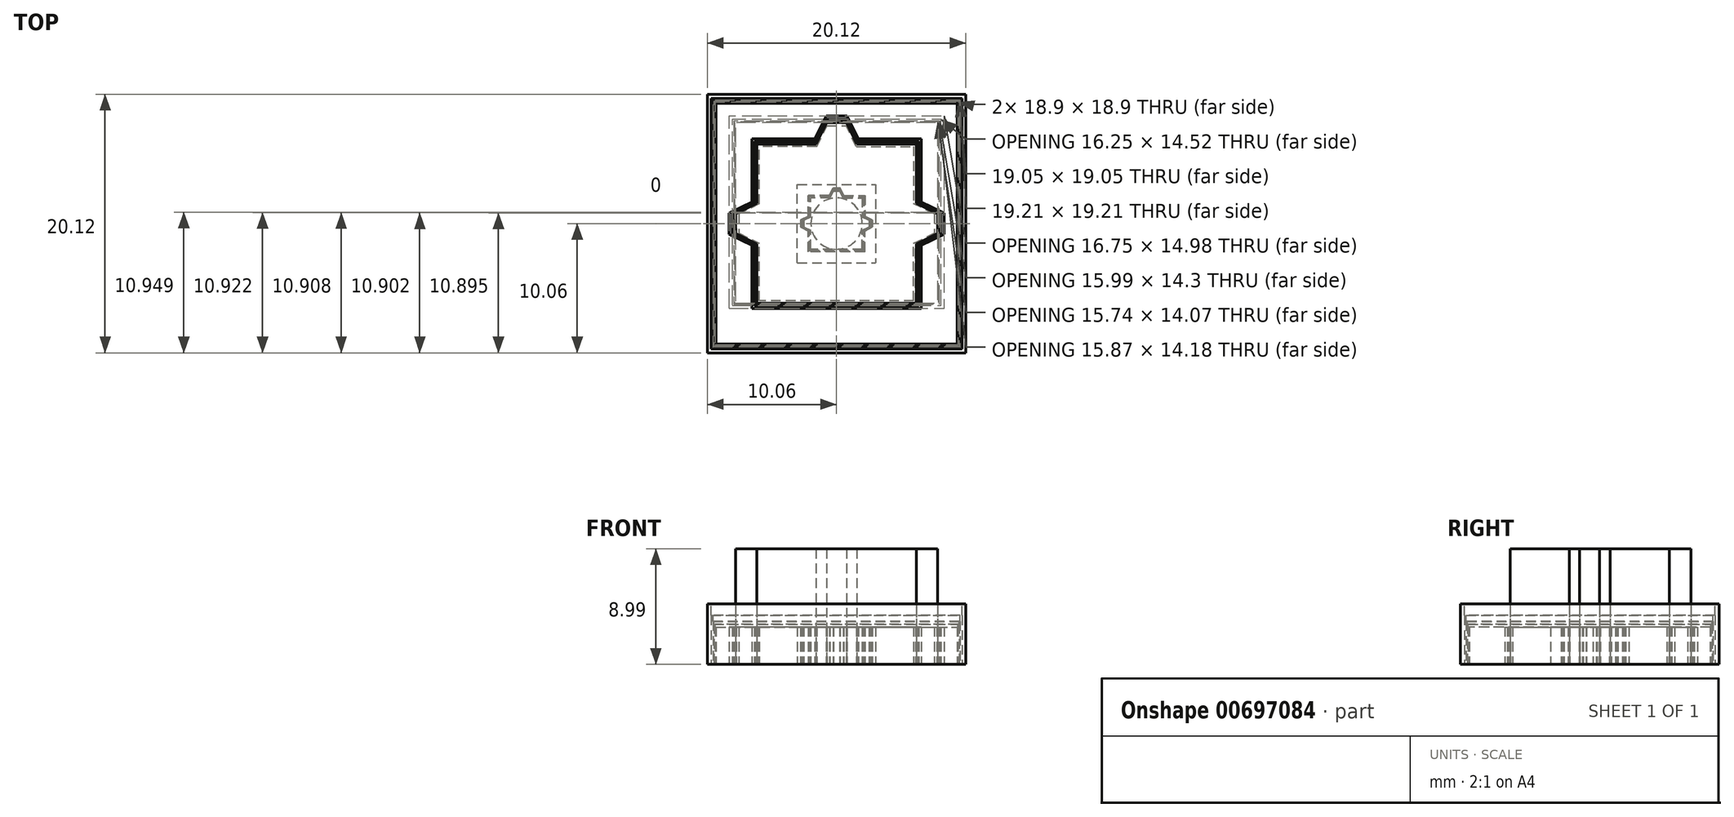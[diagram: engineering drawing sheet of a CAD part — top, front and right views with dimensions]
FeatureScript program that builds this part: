
annotation { "Feature Type Name" : "Feature", "Feature Type Description" : "" }
export const myFeature = defineFeature(function(context is Context, id is Id, definition is map)
    precondition{}
    {
        {
            assignVariable(context, id + "F0", {"name" : "pin_platform_thickness", "anyValue" : 4});
        }
        {
            assignVariable(context, id + "F1", {"name" : "pin_shaft_height", "anyValue" : 6});
        }
        {
            assignVariable(context, id + "F2", {"name" : "pin_hole_depth", "anyValue" : 5});
        }
        {
            var Q0;
            Q0=qCreatedBy(makeId("Top.planeOp"),FACE);
            var sketch = newSketch(context, id + "F3", { "sketchPlane" : qUnion([Q0])});
            skPoint(sketch, "E0.middle", {"position": v(0, 0) * mm});
            skCircle(sketch, "E1", {"center": v(0, 0) * mm, "radius": 2 * mm});
            skLineSegment(sketch, "E2", {"start": v(0, 0) * mm, "end": v(-2, 0) * mm});
            skLineSegment(sketch, "E3", {"start": v(-2, 0) * mm, "end": v(-2, 2) * mm});
            skLineSegment(sketch, "E4", {"start": v(0, 0) * mm, "end": v(0, 2) * mm});
            skLineSegment(sketch, "E5", {"start": v(0, 0) * mm, "end": v(2, 0) * mm});
            skLineSegment(sketch, "E6", {"start": v(0, 0) * mm, "end": v(0, -2) * mm});
            skLineSegment(sketch, "E7", {"start": v(0, -2) * mm, "end": v(2, 0) * mm});
            skLineSegment(sketch, "E8", {"start": v(2, 0) * mm, "end": v(0, 2) * mm});
            skLineSegment(sketch, "E9", {"start": v(0, 2) * mm, "end": v(-2, 0) * mm});
            skLineSegment(sketch, "E10", {"start": v(-2, 0) * mm, "end": v(0, -2) * mm});
            skLineSegment(sketch, "E11", {"start": v(0, -2) * mm, "end": v(-2, -2) * mm});
            skLineSegment(sketch, "E12", {"start": v(-2, -2) * mm, "end": v(-2, 0) * mm});
            skLineSegment(sketch, "E13", {"start": v(0, 2) * mm, "end": v(-2, 2) * mm});
            skLineSegment(sketch, "E14", {"start": v(0, 2) * mm, "end": v(2, 2) * mm});
            skLineSegment(sketch, "E15", {"start": v(2, 2) * mm, "end": v(2, 0) * mm});
            skLineSegment(sketch, "E16", {"start": v(2, -2) * mm, "end": v(0, -2) * mm});
            skLineSegment(sketch, "E17", {"start": v(2, -2) * mm, "end": v(2, 0) * mm});
            skLineSegment(sketch, "E18", {"start": v(0, 2) * mm, "end": v(0, 3.05) * mm});
            skLineSegment(sketch, "E19", {"start": v(0, 0) * mm, "end": v(0, 1) * mm});
            skLineSegment(sketch, "E20", {"start": v(0, 1) * mm, "end": v(1, 1) * mm});
            skLineSegment(sketch, "E21", {"start": v(1, 1) * mm, "end": v(0, 3.05) * mm});
            skLineSegment(sketch, "E22", {"start": v(0, 1) * mm, "end": v(-1, 1) * mm});
            skLineSegment(sketch, "E23", {"start": v(-1, 1) * mm, "end": v(0, 3.05) * mm});
            skLineSegment(sketch, "E24", {"start": v(1, 1) * mm, "end": v(1, 0) * mm});
            skLineSegment(sketch, "E25", {"start": v(1, 0) * mm, "end": v(1, -1) * mm});
            skLineSegment(sketch, "E26", {"start": v(1, -1) * mm, "end": v(3.05, 0) * mm});
            skLineSegment(sketch, "E27", {"start": v(3.05, 0) * mm, "end": v(1, 1) * mm});
            skLineSegment(sketch, "E28", {"start": v(1, -1) * mm, "end": v(-1, -1) * mm});
            skLineSegment(sketch, "E29", {"start": v(-1, -1) * mm, "end": v(-1, 1) * mm});
            skLineSegment(sketch, "E30", {"start": v(-1, 1) * mm, "end": v(-3.05, 0) * mm});
            skLineSegment(sketch, "E31", {"start": v(-3.05, 0) * mm, "end": v(-1, -1) * mm});
            skLineSegment(sketch, "E32", {"start": v(-1, -1) * mm, "end": v(0, -3.05) * mm});
            skLineSegment(sketch, "E33", {"start": v(0, -3.05) * mm, "end": v(1, -1) * mm});
            skLineSegment(sketch, "E34", {"start": v(2.54, 0.25) * mm, "end": v(2.54, -0.25) * mm});
            skLineSegment(sketch, "E35", {"start": v(-0.24, -2.55) * mm, "end": v(0.24, -2.55) * mm});
            skLineSegment(sketch, "E36", {"start": v(-2.54, 0.25) * mm, "end": v(-2.54, -0.25) * mm});
            skLineSegment(sketch, "E37", {"start": v(-0.25, 2.54) * mm, "end": v(0.25, 2.54) * mm});
            skLineSegment(sketch, "E38", {"start": v(-3.05, -3.05) * mm, "end": v(3.05, -3.05) * mm});
            skLineSegment(sketch, "E39", {"start": v(-3.05, -3.05) * mm, "end": v(-3.05, 3.05) * mm});
            skLineSegment(sketch, "E40", {"start": v(-3.05, 3.05) * mm, "end": v(3.05, 3.05) * mm});
            skLineSegment(sketch, "E41", {"start": v(3.05, 3.05) * mm, "end": v(3.05, -3.05) * mm});
            skCircle(sketch, "E42", {"center": v(0, 0) * mm, "radius": 0.38 * mm});
            skSolve(sketch);
        }
        {
            var Q0;
            {var subQ0=sQuery(id+"F3.wireOp",EDGE,"E23");var subQ3=sQuery(id+"F3.wireOp",EDGE,"E1");var subQ4=makeQuery(id+"F3.imprint","INTERSECT",VERTEX,{"derivedFrom":[subQ3,subQ0]});Q0=makeQuery(id+"F3.imprint","IMPRINT",FACE,{"disambiguationData":[TD([[makeQuery(id+"F3.imprint","IMPRINT",EDGE,{"disambiguationData":[TD([[subQ4,-1.0]])],"derivedFrom":subQ3}),-1.0]])]});}
            var Q1;
            {var subQ3=sQuery(id+"F3.wireOp",EDGE,"E23");var subQ5=sQuery(id+"F3.wireOp",EDGE,"E37");var subQ7=makeQuery(id+"F3.imprint","INTERSECT",VERTEX,{"derivedFrom":[subQ3,subQ5]});Q1=makeQuery(id+"F3.imprint","IMPRINT",FACE,{"disambiguationData":[TD([[makeQuery(id+"F3.imprint","IMPRINT",EDGE,{"disambiguationData":[TD([[subQ7,1.0]])],"derivedFrom":subQ3}),-1.0]])]});}
            var Q2;
            {var subQ3=sQuery(id+"F3.wireOp",EDGE,"E21");var subQ5=sQuery(id+"F3.wireOp",EDGE,"E37");var subQ6=makeQuery(id+"F3.imprint","INTERSECT",VERTEX,{"derivedFrom":[subQ3,subQ5]});Q2=makeQuery(id+"F3.imprint","IMPRINT",FACE,{"disambiguationData":[TD([[makeQuery(id+"F3.imprint","IMPRINT",EDGE,{"disambiguationData":[TD([[subQ6,1.0]])],"derivedFrom":subQ3}),1.0]])]});}
            var Q3;
            {var subQ3=sQuery(id+"F3.wireOp",EDGE,"E1");var subQ7=sQuery(id+"F3.wireOp",EDGE,"E27");var subQ9=makeQuery(id+"F3.imprint","INTERSECT",VERTEX,{"derivedFrom":[subQ3,subQ7]});Q3=makeQuery(id+"F3.imprint","IMPRINT",FACE,{"disambiguationData":[TD([[makeQuery(id+"F3.imprint","IMPRINT",EDGE,{"disambiguationData":[TD([[subQ9,-1.0]])],"derivedFrom":subQ3}),-1.0]])]});}
            var Q4;
            {var subQ0=sQuery(id+"F3.wireOp",EDGE,"E23");var subQ1=sQuery(id+"F3.wireOp",EDGE,"E1");var subQ2=makeQuery(id+"F3.imprint","INTERSECT",VERTEX,{"derivedFrom":[subQ1,subQ0]});Q4=makeQuery(id+"F3.imprint","IMPRINT",FACE,{"disambiguationData":[TD([[makeQuery(id+"F3.imprint","IMPRINT",EDGE,{"disambiguationData":[TD([[subQ2,-1.0]])],"derivedFrom":subQ1}),1.0]])]});}
            var Q5;
            {var subQ1=sQuery(id+"F3.wireOp",EDGE,"E1");var subQ3=sQuery(id+"F3.wireOp",EDGE,"E23");var subQ4=makeQuery(id+"F3.imprint","INTERSECT",VERTEX,{"derivedFrom":[subQ1,subQ3]});Q5=makeQuery(id+"F3.imprint","IMPRINT",FACE,{"disambiguationData":[TD([[makeQuery(id+"F3.imprint","IMPRINT",EDGE,{"disambiguationData":[TD([[subQ4,1.0]])],"derivedFrom":subQ3}),-1.0]])]});}
            var Q6;
            {var subQ1=sQuery(id+"F3.wireOp",EDGE,"E1");var subQ3=sQuery(id+"F3.wireOp",EDGE,"E21");var subQ4=makeQuery(id+"F3.imprint","INTERSECT",VERTEX,{"derivedFrom":[subQ1,subQ3]});Q6=makeQuery(id+"F3.imprint","IMPRINT",FACE,{"disambiguationData":[TD([[makeQuery(id+"F3.imprint","IMPRINT",EDGE,{"disambiguationData":[TD([[subQ4,1.0]])],"derivedFrom":subQ3}),1.0]])]});}
            var Q7;
            {var subQ0=sQuery(id+"F3.wireOp",EDGE,"E4");Q7=makeQuery(id+"F3.imprint","IMPRINT",FACE,{"disambiguationData":[TD([[makeQuery(id+"F3.imprint","IMPRINT",EDGE,{"derivedFrom":subQ0}),-1.0]])]});}
            var Q8;
            {var subQ0=sQuery(id+"F3.wireOp",EDGE,"E4");Q8=makeQuery(id+"F3.imprint","IMPRINT",FACE,{"disambiguationData":[TD([[makeQuery(id+"F3.imprint","IMPRINT",EDGE,{"derivedFrom":subQ0}),1.0]])]});}
            var Q9;
            {var subQ0=sQuery(id+"F3.wireOp",EDGE,"E19");Q9=makeQuery(id+"F3.imprint","IMPRINT",FACE,{"disambiguationData":[TD([[makeQuery(id+"F3.imprint","IMPRINT",EDGE,{"derivedFrom":subQ0}),1.0]])]});}
            var Q10;
            {var subQ1=sQuery(id+"F3.wireOp",EDGE,"E1");var subQ3=sQuery(id+"F3.wireOp",EDGE,"E30");var subQ4=makeQuery(id+"F3.imprint","INTERSECT",VERTEX,{"derivedFrom":[subQ1,subQ3]});Q10=makeQuery(id+"F3.imprint","IMPRINT",FACE,{"disambiguationData":[TD([[makeQuery(id+"F3.imprint","IMPRINT",EDGE,{"disambiguationData":[TD([[subQ4,1.0]])],"derivedFrom":subQ3}),1.0]])]});}
            var Q11;
            {var subQ1=sQuery(id+"F3.wireOp",EDGE,"E2");var subQ3=sQuery(id+"F3.wireOp",EDGE,"E29");var subQ4=makeQuery(id+"F3.imprint","INTERSECT",VERTEX,{"derivedFrom":[subQ1,subQ3]});Q11=makeQuery(id+"F3.imprint","IMPRINT",FACE,{"disambiguationData":[TD([[makeQuery(id+"F3.imprint","IMPRINT",EDGE,{"disambiguationData":[TD([[subQ4,-1.0]])],"derivedFrom":subQ3}),1.0]])]});}
            var Q12;
            {var subQ0=sQuery(id+"F3.wireOp",EDGE,"E19");Q12=makeQuery(id+"F3.imprint","IMPRINT",FACE,{"disambiguationData":[TD([[makeQuery(id+"F3.imprint","IMPRINT",EDGE,{"derivedFrom":subQ0}),-1.0]])]});}
            var Q13;
            {var subQ0=sQuery(id+"F3.wireOp",EDGE,"E27");var subQ1=sQuery(id+"F3.wireOp",EDGE,"E1");var subQ2=makeQuery(id+"F3.imprint","INTERSECT",VERTEX,{"derivedFrom":[subQ1,subQ0]});Q13=makeQuery(id+"F3.imprint","IMPRINT",FACE,{"disambiguationData":[TD([[makeQuery(id+"F3.imprint","IMPRINT",EDGE,{"disambiguationData":[TD([[subQ2,-1.0]])],"derivedFrom":subQ1}),1.0]])]});}
            var Q14;
            {var subQ0=sQuery(id+"F3.wireOp",EDGE,"E15");var subQ3=sQuery(id+"F3.wireOp",EDGE,"E27");var subQ5=makeQuery(id+"F3.imprint","INTERSECT",VERTEX,{"derivedFrom":[subQ0,subQ3]});Q14=makeQuery(id+"F3.imprint","IMPRINT",FACE,{"disambiguationData":[TD([[makeQuery(id+"F3.imprint","IMPRINT",EDGE,{"disambiguationData":[TD([[subQ5,-1.0]])],"derivedFrom":subQ3}),1.0]])]});}
            var Q15;
            {var subQ1=sQuery(id+"F3.wireOp",EDGE,"E1");var subQ3=sQuery(id+"F3.wireOp",EDGE,"E27");var subQ4=makeQuery(id+"F3.imprint","INTERSECT",VERTEX,{"derivedFrom":[subQ1,subQ3]});Q15=makeQuery(id+"F3.imprint","IMPRINT",FACE,{"disambiguationData":[TD([[makeQuery(id+"F3.imprint","IMPRINT",EDGE,{"disambiguationData":[TD([[subQ4,-1.0]])],"derivedFrom":subQ3}),1.0]])]});}
            var Q16;
            {var subQ3=sQuery(id+"F3.wireOp",EDGE,"E24");Q16=makeQuery(id+"F3.imprint","IMPRINT",FACE,{"disambiguationData":[TD([[makeQuery(id+"F3.imprint","IMPRINT",EDGE,{"derivedFrom":subQ3}),1.0]])]});}
            var Q17;
            {var subQ0=sQuery(id+"F3.wireOp",EDGE,"E3");var subQ3=sQuery(id+"F3.wireOp",EDGE,"E30");var subQ5=makeQuery(id+"F3.imprint","INTERSECT",VERTEX,{"derivedFrom":[subQ0,subQ3]});Q17=makeQuery(id+"F3.imprint","IMPRINT",FACE,{"disambiguationData":[TD([[makeQuery(id+"F3.imprint","IMPRINT",EDGE,{"disambiguationData":[TD([[subQ5,1.0]])],"derivedFrom":subQ3}),1.0]])]});}
            var Q18;
            {var subQ1=sQuery(id+"F3.wireOp",EDGE,"E2");var subQ3=sQuery(id+"F3.wireOp",EDGE,"E29");var subQ4=makeQuery(id+"F3.imprint","INTERSECT",VERTEX,{"derivedFrom":[subQ1,subQ3]});Q18=makeQuery(id+"F3.imprint","IMPRINT",FACE,{"disambiguationData":[TD([[makeQuery(id+"F3.imprint","IMPRINT",EDGE,{"disambiguationData":[TD([[subQ4,1.0]])],"derivedFrom":subQ3}),1.0]])]});}
            var Q19;
            {var subQ1=sQuery(id+"F3.wireOp",EDGE,"E1");var subQ3=sQuery(id+"F3.wireOp",EDGE,"E31");var subQ4=makeQuery(id+"F3.imprint","INTERSECT",VERTEX,{"derivedFrom":[subQ1,subQ3]});Q19=makeQuery(id+"F3.imprint","IMPRINT",FACE,{"disambiguationData":[TD([[makeQuery(id+"F3.imprint","IMPRINT",EDGE,{"disambiguationData":[TD([[subQ4,-1.0]])],"derivedFrom":subQ3}),1.0]])]});}
            var Q20;
            {var subQ0=sQuery(id+"F3.wireOp",EDGE,"E31");var subQ3=sQuery(id+"F3.wireOp",EDGE,"E1");var subQ4=makeQuery(id+"F3.imprint","INTERSECT",VERTEX,{"derivedFrom":[subQ3,subQ0]});Q20=makeQuery(id+"F3.imprint","IMPRINT",FACE,{"disambiguationData":[TD([[makeQuery(id+"F3.imprint","IMPRINT",EDGE,{"disambiguationData":[TD([[subQ4,-1.0]])],"derivedFrom":subQ3}),-1.0]])]});}
            var Q21;
            {var subQ0=sQuery(id+"F3.wireOp",EDGE,"E36");Q21=makeQuery(id+"F3.imprint","IMPRINT",FACE,{"disambiguationData":[TD([[makeQuery(id+"F3.imprint","IMPRINT",EDGE,{"derivedFrom":subQ0}),1.0]])]});}
            var Q22;
            {var subQ0=sQuery(id+"F3.wireOp",EDGE,"E12");var subQ3=sQuery(id+"F3.wireOp",EDGE,"E31");var subQ5=makeQuery(id+"F3.imprint","INTERSECT",VERTEX,{"derivedFrom":[subQ0,subQ3]});Q22=makeQuery(id+"F3.imprint","IMPRINT",FACE,{"disambiguationData":[TD([[makeQuery(id+"F3.imprint","IMPRINT",EDGE,{"disambiguationData":[TD([[subQ5,-1.0]])],"derivedFrom":subQ3}),1.0]])]});}
            var Q23;
            {var subQ1=sQuery(id+"F3.wireOp",EDGE,"E2");var subQ3=sQuery(id+"F3.wireOp",EDGE,"E29");var subQ4=makeQuery(id+"F3.imprint","INTERSECT",VERTEX,{"derivedFrom":[subQ1,subQ3]});Q23=makeQuery(id+"F3.imprint","IMPRINT",FACE,{"disambiguationData":[TD([[makeQuery(id+"F3.imprint","IMPRINT",EDGE,{"disambiguationData":[TD([[subQ4,1.0]])],"derivedFrom":subQ1}),1.0]])]});}
            var Q24;
            {var subQ3=sQuery(id+"F3.wireOp",EDGE,"E25");Q24=makeQuery(id+"F3.imprint","IMPRINT",FACE,{"disambiguationData":[TD([[makeQuery(id+"F3.imprint","IMPRINT",EDGE,{"derivedFrom":subQ3}),-1.0]])]});}
            var Q25;
            {var subQ1=sQuery(id+"F3.wireOp",EDGE,"E6");var subQ3=sQuery(id+"F3.wireOp",EDGE,"E28");var subQ4=makeQuery(id+"F3.imprint","INTERSECT",VERTEX,{"derivedFrom":[subQ1,subQ3]});Q25=makeQuery(id+"F3.imprint","IMPRINT",FACE,{"disambiguationData":[TD([[makeQuery(id+"F3.imprint","IMPRINT",EDGE,{"disambiguationData":[TD([[subQ4,1.0]])],"derivedFrom":subQ3}),1.0]])]});}
            var Q26;
            {var subQ1=sQuery(id+"F3.wireOp",EDGE,"E6");var subQ3=sQuery(id+"F3.wireOp",EDGE,"E28");var subQ4=makeQuery(id+"F3.imprint","INTERSECT",VERTEX,{"derivedFrom":[subQ1,subQ3]});Q26=makeQuery(id+"F3.imprint","IMPRINT",FACE,{"disambiguationData":[TD([[makeQuery(id+"F3.imprint","IMPRINT",EDGE,{"disambiguationData":[TD([[subQ4,-1.0]])],"derivedFrom":subQ3}),1.0]])]});}
            var Q27;
            {var subQ1=sQuery(id+"F3.wireOp",EDGE,"E1");var subQ3=sQuery(id+"F3.wireOp",EDGE,"E32");var subQ4=makeQuery(id+"F3.imprint","INTERSECT",VERTEX,{"derivedFrom":[subQ1,subQ3]});Q27=makeQuery(id+"F3.imprint","IMPRINT",FACE,{"disambiguationData":[TD([[makeQuery(id+"F3.imprint","IMPRINT",EDGE,{"disambiguationData":[TD([[subQ4,1.0]])],"derivedFrom":subQ3}),1.0]])]});}
            var Q28;
            {var subQ0=sQuery(id+"F3.wireOp",EDGE,"E31");var subQ1=sQuery(id+"F3.wireOp",EDGE,"E1");var subQ2=makeQuery(id+"F3.imprint","INTERSECT",VERTEX,{"derivedFrom":[subQ1,subQ0]});Q28=makeQuery(id+"F3.imprint","IMPRINT",FACE,{"disambiguationData":[TD([[makeQuery(id+"F3.imprint","IMPRINT",EDGE,{"disambiguationData":[TD([[subQ2,-1.0]])],"derivedFrom":subQ1}),1.0]])]});}
            var Q29;
            {var subQ1=sQuery(id+"F3.wireOp",EDGE,"E1");var subQ3=sQuery(id+"F3.wireOp",EDGE,"E33");var subQ4=makeQuery(id+"F3.imprint","INTERSECT",VERTEX,{"derivedFrom":[subQ1,subQ3]});Q29=makeQuery(id+"F3.imprint","IMPRINT",FACE,{"disambiguationData":[TD([[makeQuery(id+"F3.imprint","IMPRINT",EDGE,{"disambiguationData":[TD([[subQ4,-1.0]])],"derivedFrom":subQ3}),1.0]])]});}
            var Q30;
            {var subQ0=sQuery(id+"F3.wireOp",EDGE,"E33");var subQ1=sQuery(id+"F3.wireOp",EDGE,"E1");var subQ2=makeQuery(id+"F3.imprint","INTERSECT",VERTEX,{"derivedFrom":[subQ1,subQ0]});Q30=makeQuery(id+"F3.imprint","IMPRINT",FACE,{"disambiguationData":[TD([[makeQuery(id+"F3.imprint","IMPRINT",EDGE,{"disambiguationData":[TD([[subQ2,-1.0]])],"derivedFrom":subQ1}),1.0]])]});}
            var Q31;
            {var subQ1=sQuery(id+"F3.wireOp",EDGE,"E1");var subQ3=sQuery(id+"F3.wireOp",EDGE,"E26");var subQ4=makeQuery(id+"F3.imprint","INTERSECT",VERTEX,{"derivedFrom":[subQ1,subQ3]});Q31=makeQuery(id+"F3.imprint","IMPRINT",FACE,{"disambiguationData":[TD([[makeQuery(id+"F3.imprint","IMPRINT",EDGE,{"disambiguationData":[TD([[subQ4,1.0]])],"derivedFrom":subQ3}),1.0]])]});}
            var Q32;
            {var subQ3=sQuery(id+"F3.wireOp",EDGE,"E25");Q32=makeQuery(id+"F3.imprint","IMPRINT",FACE,{"disambiguationData":[TD([[makeQuery(id+"F3.imprint","IMPRINT",EDGE,{"derivedFrom":subQ3}),1.0]])]});}
            var Q33;
            {var subQ0=sQuery(id+"F3.wireOp",EDGE,"E17");var subQ3=sQuery(id+"F3.wireOp",EDGE,"E26");var subQ5=makeQuery(id+"F3.imprint","INTERSECT",VERTEX,{"derivedFrom":[subQ0,subQ3]});Q33=makeQuery(id+"F3.imprint","IMPRINT",FACE,{"disambiguationData":[TD([[makeQuery(id+"F3.imprint","IMPRINT",EDGE,{"disambiguationData":[TD([[subQ5,1.0]])],"derivedFrom":subQ3}),1.0]])]});}
            var Q34;
            {var subQ0=sQuery(id+"F3.wireOp",EDGE,"E34");Q34=makeQuery(id+"F3.imprint","IMPRINT",FACE,{"disambiguationData":[TD([[makeQuery(id+"F3.imprint","IMPRINT",EDGE,{"derivedFrom":subQ0}),-1.0]])]});}
            var Q35;
            {var subQ5=sQuery(id+"F3.wireOp",EDGE,"E1");var subQ7=sQuery(id+"F3.wireOp",EDGE,"E33");var subQ9=makeQuery(id+"F3.imprint","INTERSECT",VERTEX,{"derivedFrom":[subQ5,subQ7]});Q35=makeQuery(id+"F3.imprint","IMPRINT",FACE,{"disambiguationData":[TD([[makeQuery(id+"F3.imprint","IMPRINT",EDGE,{"disambiguationData":[TD([[subQ9,-1.0]])],"derivedFrom":subQ5}),-1.0]])]});}
            var Q36;
            {var subQ0=sQuery(id+"F3.wireOp",EDGE,"E35");Q36=makeQuery(id+"F3.imprint","IMPRINT",FACE,{"disambiguationData":[TD([[makeQuery(id+"F3.imprint","IMPRINT",EDGE,{"derivedFrom":subQ0}),1.0]])]});}
            var Q37;
            {var subQ0=sQuery(id+"F3.wireOp",EDGE,"E16");var subQ3=sQuery(id+"F3.wireOp",EDGE,"E33");var subQ5=makeQuery(id+"F3.imprint","INTERSECT",VERTEX,{"derivedFrom":[subQ0,subQ3]});Q37=makeQuery(id+"F3.imprint","IMPRINT",FACE,{"disambiguationData":[TD([[makeQuery(id+"F3.imprint","IMPRINT",EDGE,{"disambiguationData":[TD([[subQ5,-1.0]])],"derivedFrom":subQ3}),1.0]])]});}
            var Q38;
            {var subQ0=sQuery(id+"F3.wireOp",EDGE,"E11");var subQ3=sQuery(id+"F3.wireOp",EDGE,"E32");var subQ5=makeQuery(id+"F3.imprint","INTERSECT",VERTEX,{"derivedFrom":[subQ0,subQ3]});Q38=makeQuery(id+"F3.imprint","IMPRINT",FACE,{"disambiguationData":[TD([[makeQuery(id+"F3.imprint","IMPRINT",EDGE,{"disambiguationData":[TD([[subQ5,1.0]])],"derivedFrom":subQ3}),1.0]])]});}
            var Q39;
            {var subQ0=sQuery(id+"F3.wireOp",EDGE,"E14");var subQ3=sQuery(id+"F3.wireOp",EDGE,"E21");var subQ5=makeQuery(id+"F3.imprint","INTERSECT",VERTEX,{"derivedFrom":[subQ0,subQ3]});Q39=makeQuery(id+"F3.imprint","IMPRINT",FACE,{"disambiguationData":[TD([[makeQuery(id+"F3.imprint","IMPRINT",EDGE,{"disambiguationData":[TD([[subQ5,1.0]])],"derivedFrom":subQ3}),1.0]])]});}
            var Q40;
            {var subQ0=sQuery(id+"F3.wireOp",EDGE,"E13");var subQ3=sQuery(id+"F3.wireOp",EDGE,"E23");var subQ5=makeQuery(id+"F3.imprint","INTERSECT",VERTEX,{"derivedFrom":[subQ0,subQ3]});Q40=makeQuery(id+"F3.imprint","IMPRINT",FACE,{"disambiguationData":[TD([[makeQuery(id+"F3.imprint","IMPRINT",EDGE,{"disambiguationData":[TD([[subQ5,1.0]])],"derivedFrom":subQ3}),-1.0]])]});}
            extrude(context, id + "F4", {"entities" : qUnion([Q0, Q1, Q2, Q3, Q4, Q5, Q6, Q7, Q8, Q9, Q10, Q11, Q12, Q13, Q14, Q15, Q16, Q17, Q18, Q19, Q20, Q21, Q22, Q23, Q24, Q25, Q26, Q27, Q28, Q29, Q30, Q31, Q32, Q33, Q34, Q35, Q36, Q37, Q38, Q39, Q40]), "depth" : (getVariable(context, 'pin_platform_thickness')) * mm, "offsetDistance" : 25 * mm});
        }
        {
            var Q0;
            Q0=makeQuery(id+"F4.opExtrude","SWEPT_BODY",BODY,{"disambiguationData":[OSD([sQuery(id+"F3.wireOp",EDGE,"E3"),sQuery(id+"F3.wireOp",EDGE,"E11"),sQuery(id+"F3.wireOp",EDGE,"E12"),sQuery(id+"F3.wireOp",EDGE,"E13"),sQuery(id+"F3.wireOp",EDGE,"E14"),sQuery(id+"F3.wireOp",EDGE,"E15"),sQuery(id+"F3.wireOp",EDGE,"E16"),sQuery(id+"F3.wireOp",EDGE,"E17"),sQuery(id+"F3.wireOp",EDGE,"E21"),sQuery(id+"F3.wireOp",EDGE,"E23"),sQuery(id+"F3.wireOp",EDGE,"E26"),sQuery(id+"F3.wireOp",EDGE,"E27"),sQuery(id+"F3.wireOp",EDGE,"E30"),sQuery(id+"F3.wireOp",EDGE,"E31"),sQuery(id+"F3.wireOp",EDGE,"E32"),sQuery(id+"F3.wireOp",EDGE,"E33"),sQuery(id+"F3.wireOp",EDGE,"E34"),sQuery(id+"F3.wireOp",EDGE,"E35"),sQuery(id+"F3.wireOp",EDGE,"E36"),sQuery(id+"F3.wireOp",EDGE,"E37")])]});
            transform(context, id + "F5", {"entities" : qUnion([Q0]), "transformType" : TransformType.TRANSLATION_3D, "dx" : 0 * mm, "dy" : 0 * mm, "dz" : 0 * mm, "makeCopy" : true});
        }
        {
            var Q0;
            Q0=makeQuery(id+"F5.opPattern","COPY",BODY,{"derivedFrom":makeQuery(id+"F4.opExtrude","SWEPT_BODY",BODY,{"disambiguationData":[OSD([sQuery(id+"F3.wireOp",EDGE,"E3"),sQuery(id+"F3.wireOp",EDGE,"E11"),sQuery(id+"F3.wireOp",EDGE,"E12"),sQuery(id+"F3.wireOp",EDGE,"E13"),sQuery(id+"F3.wireOp",EDGE,"E14"),sQuery(id+"F3.wireOp",EDGE,"E15"),sQuery(id+"F3.wireOp",EDGE,"E16"),sQuery(id+"F3.wireOp",EDGE,"E17"),sQuery(id+"F3.wireOp",EDGE,"E21"),sQuery(id+"F3.wireOp",EDGE,"E23"),sQuery(id+"F3.wireOp",EDGE,"E26"),sQuery(id+"F3.wireOp",EDGE,"E27"),sQuery(id+"F3.wireOp",EDGE,"E30"),sQuery(id+"F3.wireOp",EDGE,"E31"),sQuery(id+"F3.wireOp",EDGE,"E32"),sQuery(id+"F3.wireOp",EDGE,"E33"),sQuery(id+"F3.wireOp",EDGE,"E34"),sQuery(id+"F3.wireOp",EDGE,"E35"),sQuery(id+"F3.wireOp",EDGE,"E36"),sQuery(id+"F3.wireOp",EDGE,"E37")])]}),"instanceName":"1"});
            var Q1;
            Q1=sQuery(id+"F3.wireOp",VERTEX,"E0.middle");
            transform(context, id + "F6", {"entities" : qUnion([Q0]), "transformType" : TransformType.SCALE_UNIFORMLY, "scale" : 1.1, "scalePoint" : qUnion([Q1]), "makeCopy" : false});
        }
        {
            var Q0;
            Q0=makeQuery(id+"F4.opExtrude","SWEPT_BODY",BODY,{"disambiguationData":[OSD([sQuery(id+"F3.wireOp",EDGE,"E3"),sQuery(id+"F3.wireOp",EDGE,"E11"),sQuery(id+"F3.wireOp",EDGE,"E12"),sQuery(id+"F3.wireOp",EDGE,"E13"),sQuery(id+"F3.wireOp",EDGE,"E14"),sQuery(id+"F3.wireOp",EDGE,"E15"),sQuery(id+"F3.wireOp",EDGE,"E16"),sQuery(id+"F3.wireOp",EDGE,"E17"),sQuery(id+"F3.wireOp",EDGE,"E21"),sQuery(id+"F3.wireOp",EDGE,"E23"),sQuery(id+"F3.wireOp",EDGE,"E26"),sQuery(id+"F3.wireOp",EDGE,"E27"),sQuery(id+"F3.wireOp",EDGE,"E30"),sQuery(id+"F3.wireOp",EDGE,"E31"),sQuery(id+"F3.wireOp",EDGE,"E32"),sQuery(id+"F3.wireOp",EDGE,"E33"),sQuery(id+"F3.wireOp",EDGE,"E34"),sQuery(id+"F3.wireOp",EDGE,"E35"),sQuery(id+"F3.wireOp",EDGE,"E36"),sQuery(id+"F3.wireOp",EDGE,"E37")])]});
            var Q1;
            Q1=makeQuery(id+"F5.opPattern","COPY",BODY,{"derivedFrom":makeQuery(id+"F4.opExtrude","SWEPT_BODY",BODY,{"disambiguationData":[OSD([sQuery(id+"F3.wireOp",EDGE,"E3"),sQuery(id+"F3.wireOp",EDGE,"E11"),sQuery(id+"F3.wireOp",EDGE,"E12"),sQuery(id+"F3.wireOp",EDGE,"E13"),sQuery(id+"F3.wireOp",EDGE,"E14"),sQuery(id+"F3.wireOp",EDGE,"E15"),sQuery(id+"F3.wireOp",EDGE,"E16"),sQuery(id+"F3.wireOp",EDGE,"E17"),sQuery(id+"F3.wireOp",EDGE,"E21"),sQuery(id+"F3.wireOp",EDGE,"E23"),sQuery(id+"F3.wireOp",EDGE,"E26"),sQuery(id+"F3.wireOp",EDGE,"E27"),sQuery(id+"F3.wireOp",EDGE,"E30"),sQuery(id+"F3.wireOp",EDGE,"E31"),sQuery(id+"F3.wireOp",EDGE,"E32"),sQuery(id+"F3.wireOp",EDGE,"E33"),sQuery(id+"F3.wireOp",EDGE,"E34"),sQuery(id+"F3.wireOp",EDGE,"E35"),sQuery(id+"F3.wireOp",EDGE,"E36"),sQuery(id+"F3.wireOp",EDGE,"E37")])]}),"instanceName":"1"});
            booleanBodies(context, id + "F7", {"operationType" : BooleanOperationType.SUBTRACTION, "tools" : qUnion([Q0]), "targets" : qUnion([Q1])});
        }
        {
            var Q0;
            Q0=makeQuery(id+"F5.opPattern","COPY",BODY,{"derivedFrom":makeQuery(id+"F4.opExtrude","SWEPT_BODY",BODY,{"disambiguationData":[OSD([sQuery(id+"F3.wireOp",EDGE,"E3"),sQuery(id+"F3.wireOp",EDGE,"E11"),sQuery(id+"F3.wireOp",EDGE,"E12"),sQuery(id+"F3.wireOp",EDGE,"E13"),sQuery(id+"F3.wireOp",EDGE,"E14"),sQuery(id+"F3.wireOp",EDGE,"E15"),sQuery(id+"F3.wireOp",EDGE,"E16"),sQuery(id+"F3.wireOp",EDGE,"E17"),sQuery(id+"F3.wireOp",EDGE,"E21"),sQuery(id+"F3.wireOp",EDGE,"E23"),sQuery(id+"F3.wireOp",EDGE,"E26"),sQuery(id+"F3.wireOp",EDGE,"E27"),sQuery(id+"F3.wireOp",EDGE,"E30"),sQuery(id+"F3.wireOp",EDGE,"E31"),sQuery(id+"F3.wireOp",EDGE,"E32"),sQuery(id+"F3.wireOp",EDGE,"E33"),sQuery(id+"F3.wireOp",EDGE,"E34"),sQuery(id+"F3.wireOp",EDGE,"E35"),sQuery(id+"F3.wireOp",EDGE,"E36"),sQuery(id+"F3.wireOp",EDGE,"E37")])]}),"instanceName":"1"});
            deleteBodies(context, id + "F8", {"entities" : qUnion([Q0])});
        }
        {
            var Q0;
            Q0 = qSketchRegion(id + "F3", true);
            var Q1;
            {var subQ0=sQuery(id+"F3.wireOp",EDGE,"E31");var subQ1=sQuery(id+"F3.wireOp",EDGE,"E1");var subQ2=makeQuery(id+"F3.imprint","INTERSECT",VERTEX,{"derivedFrom":[subQ1,subQ0]});Q1=makeQuery(id+"F3.imprint","IMPRINT",FACE,{"disambiguationData":[TD([[makeQuery(id+"F3.imprint","IMPRINT",EDGE,{"disambiguationData":[TD([[subQ2,-1.0]])],"derivedFrom":subQ1}),-1.0]])]});}
            var Q2;
            {var subQ1=sQuery(id+"F3.wireOp",EDGE,"E1");var subQ3=sQuery(id+"F3.wireOp",EDGE,"E32");var subQ4=makeQuery(id+"F3.imprint","INTERSECT",VERTEX,{"derivedFrom":[subQ1,subQ3]});Q2=makeQuery(id+"F3.imprint","IMPRINT",FACE,{"disambiguationData":[TD([[makeQuery(id+"F3.imprint","IMPRINT",EDGE,{"disambiguationData":[TD([[subQ4,1.0]])],"derivedFrom":subQ3}),1.0]])]});}
            var Q3;
            {var subQ1=sQuery(id+"F3.wireOp",EDGE,"E1");var subQ3=sQuery(id+"F3.wireOp",EDGE,"E33");var subQ4=makeQuery(id+"F3.imprint","INTERSECT",VERTEX,{"derivedFrom":[subQ1,subQ3]});Q3=makeQuery(id+"F3.imprint","IMPRINT",FACE,{"disambiguationData":[TD([[makeQuery(id+"F3.imprint","IMPRINT",EDGE,{"disambiguationData":[TD([[subQ4,-1.0]])],"derivedFrom":subQ3}),1.0]])]});}
            var Q4;
            {var subQ0=sQuery(id+"F3.wireOp",EDGE,"E33");var subQ1=sQuery(id+"F3.wireOp",EDGE,"E1");var subQ2=makeQuery(id+"F3.imprint","INTERSECT",VERTEX,{"derivedFrom":[subQ1,subQ0]});Q4=makeQuery(id+"F3.imprint","IMPRINT",FACE,{"disambiguationData":[TD([[makeQuery(id+"F3.imprint","IMPRINT",EDGE,{"disambiguationData":[TD([[subQ2,-1.0]])],"derivedFrom":subQ1}),1.0]])]});}
            var Q5;
            {var subQ5=sQuery(id+"F3.wireOp",EDGE,"E1");var subQ7=sQuery(id+"F3.wireOp",EDGE,"E33");var subQ9=makeQuery(id+"F3.imprint","INTERSECT",VERTEX,{"derivedFrom":[subQ5,subQ7]});Q5=makeQuery(id+"F3.imprint","IMPRINT",FACE,{"disambiguationData":[TD([[makeQuery(id+"F3.imprint","IMPRINT",EDGE,{"disambiguationData":[TD([[subQ9,-1.0]])],"derivedFrom":subQ5}),-1.0]])]});}
            var Q6;
            {var subQ0=sQuery(id+"F3.wireOp",EDGE,"E31");var subQ1=sQuery(id+"F3.wireOp",EDGE,"E1");var subQ2=makeQuery(id+"F3.imprint","INTERSECT",VERTEX,{"derivedFrom":[subQ1,subQ0]});Q6=makeQuery(id+"F3.imprint","IMPRINT",FACE,{"disambiguationData":[TD([[makeQuery(id+"F3.imprint","IMPRINT",EDGE,{"disambiguationData":[TD([[subQ2,-1.0]])],"derivedFrom":subQ1}),1.0]])]});}
            var Q7;
            {var subQ0=sQuery(id+"F3.wireOp",EDGE,"E19");Q7=makeQuery(id+"F3.imprint","IMPRINT",FACE,{"disambiguationData":[TD([[makeQuery(id+"F3.imprint","IMPRINT",EDGE,{"derivedFrom":subQ0}),-1.0]])]});}
            var Q8;
            {var subQ0=sQuery(id+"F3.wireOp",EDGE,"E19");Q8=makeQuery(id+"F3.imprint","IMPRINT",FACE,{"disambiguationData":[TD([[makeQuery(id+"F3.imprint","IMPRINT",EDGE,{"derivedFrom":subQ0}),1.0]])]});}
            var Q9;
            {var subQ1=sQuery(id+"F3.wireOp",EDGE,"E2");var subQ3=sQuery(id+"F3.wireOp",EDGE,"E29");var subQ4=makeQuery(id+"F3.imprint","INTERSECT",VERTEX,{"derivedFrom":[subQ1,subQ3]});Q9=makeQuery(id+"F3.imprint","IMPRINT",FACE,{"disambiguationData":[TD([[makeQuery(id+"F3.imprint","IMPRINT",EDGE,{"disambiguationData":[TD([[subQ4,-1.0]])],"derivedFrom":subQ3}),1.0]])]});}
            var Q10;
            {var subQ1=sQuery(id+"F3.wireOp",EDGE,"E1");var subQ3=sQuery(id+"F3.wireOp",EDGE,"E30");var subQ4=makeQuery(id+"F3.imprint","INTERSECT",VERTEX,{"derivedFrom":[subQ1,subQ3]});Q10=makeQuery(id+"F3.imprint","IMPRINT",FACE,{"disambiguationData":[TD([[makeQuery(id+"F3.imprint","IMPRINT",EDGE,{"disambiguationData":[TD([[subQ4,1.0]])],"derivedFrom":subQ3}),1.0]])]});}
            var Q11;
            {var subQ0=sQuery(id+"F3.wireOp",EDGE,"E23");var subQ1=sQuery(id+"F3.wireOp",EDGE,"E1");var subQ2=makeQuery(id+"F3.imprint","INTERSECT",VERTEX,{"derivedFrom":[subQ1,subQ0]});Q11=makeQuery(id+"F3.imprint","IMPRINT",FACE,{"disambiguationData":[TD([[makeQuery(id+"F3.imprint","IMPRINT",EDGE,{"disambiguationData":[TD([[subQ2,-1.0]])],"derivedFrom":subQ1}),1.0]])]});}
            var Q12;
            {var subQ0=sQuery(id+"F3.wireOp",EDGE,"E23");var subQ1=sQuery(id+"F3.wireOp",EDGE,"E1");var subQ2=makeQuery(id+"F3.imprint","INTERSECT",VERTEX,{"derivedFrom":[subQ1,subQ0]});Q12=makeQuery(id+"F3.imprint","IMPRINT",FACE,{"disambiguationData":[TD([[makeQuery(id+"F3.imprint","IMPRINT",EDGE,{"disambiguationData":[TD([[subQ2,-1.0]])],"derivedFrom":subQ1}),-1.0]])]});}
            var Q13;
            {var subQ1=sQuery(id+"F3.wireOp",EDGE,"E1");var subQ3=sQuery(id+"F3.wireOp",EDGE,"E23");var subQ4=makeQuery(id+"F3.imprint","INTERSECT",VERTEX,{"derivedFrom":[subQ1,subQ3]});Q13=makeQuery(id+"F3.imprint","IMPRINT",FACE,{"disambiguationData":[TD([[makeQuery(id+"F3.imprint","IMPRINT",EDGE,{"disambiguationData":[TD([[subQ4,1.0]])],"derivedFrom":subQ3}),-1.0]])]});}
            var Q14;
            {var subQ3=sQuery(id+"F3.wireOp",EDGE,"E23");var subQ5=sQuery(id+"F3.wireOp",EDGE,"E37");var subQ7=makeQuery(id+"F3.imprint","INTERSECT",VERTEX,{"derivedFrom":[subQ3,subQ5]});Q14=makeQuery(id+"F3.imprint","IMPRINT",FACE,{"disambiguationData":[TD([[makeQuery(id+"F3.imprint","IMPRINT",EDGE,{"disambiguationData":[TD([[subQ7,1.0]])],"derivedFrom":subQ3}),-1.0]])]});}
            var Q15;
            {var subQ1=sQuery(id+"F3.wireOp",EDGE,"E1");var subQ3=sQuery(id+"F3.wireOp",EDGE,"E21");var subQ4=makeQuery(id+"F3.imprint","INTERSECT",VERTEX,{"derivedFrom":[subQ1,subQ3]});Q15=makeQuery(id+"F3.imprint","IMPRINT",FACE,{"disambiguationData":[TD([[makeQuery(id+"F3.imprint","IMPRINT",EDGE,{"disambiguationData":[TD([[subQ4,1.0]])],"derivedFrom":subQ3}),1.0]])]});}
            var Q16;
            {var subQ0=sQuery(id+"F3.wireOp",EDGE,"E4");Q16=makeQuery(id+"F3.imprint","IMPRINT",FACE,{"disambiguationData":[TD([[makeQuery(id+"F3.imprint","IMPRINT",EDGE,{"derivedFrom":subQ0}),-1.0]])]});}
            var Q17;
            {var subQ0=sQuery(id+"F3.wireOp",EDGE,"E4");Q17=makeQuery(id+"F3.imprint","IMPRINT",FACE,{"disambiguationData":[TD([[makeQuery(id+"F3.imprint","IMPRINT",EDGE,{"derivedFrom":subQ0}),1.0]])]});}
            var Q18;
            {var subQ0=sQuery(id+"F3.wireOp",EDGE,"E27");var subQ1=sQuery(id+"F3.wireOp",EDGE,"E1");var subQ2=makeQuery(id+"F3.imprint","INTERSECT",VERTEX,{"derivedFrom":[subQ1,subQ0]});Q18=makeQuery(id+"F3.imprint","IMPRINT",FACE,{"disambiguationData":[TD([[makeQuery(id+"F3.imprint","IMPRINT",EDGE,{"disambiguationData":[TD([[subQ2,-1.0]])],"derivedFrom":subQ1}),1.0]])]});}
            var Q19;
            {var subQ1=sQuery(id+"F3.wireOp",EDGE,"E1");var subQ7=sQuery(id+"F3.wireOp",EDGE,"E27");var subQ9=makeQuery(id+"F3.imprint","INTERSECT",VERTEX,{"derivedFrom":[subQ1,subQ7]});Q19=makeQuery(id+"F3.imprint","IMPRINT",FACE,{"disambiguationData":[TD([[makeQuery(id+"F3.imprint","IMPRINT",EDGE,{"disambiguationData":[TD([[subQ9,-1.0]])],"derivedFrom":subQ1}),-1.0]])]});}
            var Q20;
            {var subQ3=sQuery(id+"F3.wireOp",EDGE,"E24");Q20=makeQuery(id+"F3.imprint","IMPRINT",FACE,{"disambiguationData":[TD([[makeQuery(id+"F3.imprint","IMPRINT",EDGE,{"derivedFrom":subQ3}),1.0]])]});}
            var Q21;
            {var subQ1=sQuery(id+"F3.wireOp",EDGE,"E1");var subQ3=sQuery(id+"F3.wireOp",EDGE,"E27");var subQ4=makeQuery(id+"F3.imprint","INTERSECT",VERTEX,{"derivedFrom":[subQ1,subQ3]});Q21=makeQuery(id+"F3.imprint","IMPRINT",FACE,{"disambiguationData":[TD([[makeQuery(id+"F3.imprint","IMPRINT",EDGE,{"disambiguationData":[TD([[subQ4,-1.0]])],"derivedFrom":subQ3}),1.0]])]});}
            var Q22;
            {var subQ1=sQuery(id+"F3.wireOp",EDGE,"E1");var subQ3=sQuery(id+"F3.wireOp",EDGE,"E26");var subQ4=makeQuery(id+"F3.imprint","INTERSECT",VERTEX,{"derivedFrom":[subQ1,subQ3]});Q22=makeQuery(id+"F3.imprint","IMPRINT",FACE,{"disambiguationData":[TD([[makeQuery(id+"F3.imprint","IMPRINT",EDGE,{"disambiguationData":[TD([[subQ4,1.0]])],"derivedFrom":subQ3}),1.0]])]});}
            var Q23;
            {var subQ3=sQuery(id+"F3.wireOp",EDGE,"E25");Q23=makeQuery(id+"F3.imprint","IMPRINT",FACE,{"disambiguationData":[TD([[makeQuery(id+"F3.imprint","IMPRINT",EDGE,{"derivedFrom":subQ3}),1.0]])]});}
            var Q24;
            {var subQ3=sQuery(id+"F3.wireOp",EDGE,"E21");var subQ5=sQuery(id+"F3.wireOp",EDGE,"E37");var subQ6=makeQuery(id+"F3.imprint","INTERSECT",VERTEX,{"derivedFrom":[subQ3,subQ5]});Q24=makeQuery(id+"F3.imprint","IMPRINT",FACE,{"disambiguationData":[TD([[makeQuery(id+"F3.imprint","IMPRINT",EDGE,{"disambiguationData":[TD([[subQ6,1.0]])],"derivedFrom":subQ3}),1.0]])]});}
            var Q25;
            {var subQ1=sQuery(id+"F3.wireOp",EDGE,"E1");var subQ3=sQuery(id+"F3.wireOp",EDGE,"E21");var subQ4=makeQuery(id+"F3.imprint","INTERSECT",VERTEX,{"derivedFrom":[subQ1,subQ3]});Q25=makeQuery(id+"F3.imprint","IMPRINT",FACE,{"disambiguationData":[TD([[makeQuery(id+"F3.imprint","IMPRINT",EDGE,{"disambiguationData":[TD([[subQ4,-1.0]])],"derivedFrom":subQ3}),1.0]])]});}
            var Q26;
            {var subQ1=sQuery(id+"F3.wireOp",EDGE,"E1");var subQ3=sQuery(id+"F3.wireOp",EDGE,"E23");var subQ4=makeQuery(id+"F3.imprint","INTERSECT",VERTEX,{"derivedFrom":[subQ1,subQ3]});Q26=makeQuery(id+"F3.imprint","IMPRINT",FACE,{"disambiguationData":[TD([[makeQuery(id+"F3.imprint","IMPRINT",EDGE,{"disambiguationData":[TD([[subQ4,-1.0]])],"derivedFrom":subQ3}),-1.0]])]});}
            var Q27;
            {var subQ1=sQuery(id+"F3.wireOp",EDGE,"E1");var subQ3=sQuery(id+"F3.wireOp",EDGE,"E27");var subQ4=makeQuery(id+"F3.imprint","INTERSECT",VERTEX,{"derivedFrom":[subQ1,subQ3]});Q27=makeQuery(id+"F3.imprint","IMPRINT",FACE,{"disambiguationData":[TD([[makeQuery(id+"F3.imprint","IMPRINT",EDGE,{"disambiguationData":[TD([[subQ4,1.0]])],"derivedFrom":subQ3}),1.0]])]});}
            var Q28;
            {var subQ1=sQuery(id+"F3.wireOp",EDGE,"E1");var subQ3=sQuery(id+"F3.wireOp",EDGE,"E26");var subQ4=makeQuery(id+"F3.imprint","INTERSECT",VERTEX,{"derivedFrom":[subQ1,subQ3]});Q28=makeQuery(id+"F3.imprint","IMPRINT",FACE,{"disambiguationData":[TD([[makeQuery(id+"F3.imprint","IMPRINT",EDGE,{"disambiguationData":[TD([[subQ4,-1.0]])],"derivedFrom":subQ3}),1.0]])]});}
            var Q29;
            {var subQ3=sQuery(id+"F3.wireOp",EDGE,"E25");Q29=makeQuery(id+"F3.imprint","IMPRINT",FACE,{"disambiguationData":[TD([[makeQuery(id+"F3.imprint","IMPRINT",EDGE,{"derivedFrom":subQ3}),-1.0]])]});}
            var Q30;
            {var subQ1=sQuery(id+"F3.wireOp",EDGE,"E6");var subQ3=sQuery(id+"F3.wireOp",EDGE,"E28");var subQ4=makeQuery(id+"F3.imprint","INTERSECT",VERTEX,{"derivedFrom":[subQ1,subQ3]});Q30=makeQuery(id+"F3.imprint","IMPRINT",FACE,{"disambiguationData":[TD([[makeQuery(id+"F3.imprint","IMPRINT",EDGE,{"disambiguationData":[TD([[subQ4,-1.0]])],"derivedFrom":subQ3}),1.0]])]});}
            var Q31;
            {var subQ1=sQuery(id+"F3.wireOp",EDGE,"E1");var subQ3=sQuery(id+"F3.wireOp",EDGE,"E31");var subQ4=makeQuery(id+"F3.imprint","INTERSECT",VERTEX,{"derivedFrom":[subQ1,subQ3]});Q31=makeQuery(id+"F3.imprint","IMPRINT",FACE,{"disambiguationData":[TD([[makeQuery(id+"F3.imprint","IMPRINT",EDGE,{"disambiguationData":[TD([[subQ4,-1.0]])],"derivedFrom":subQ3}),1.0]])]});}
            var Q32;
            {var subQ0=sQuery(id+"F3.wireOp",EDGE,"E36");Q32=makeQuery(id+"F3.imprint","IMPRINT",FACE,{"disambiguationData":[TD([[makeQuery(id+"F3.imprint","IMPRINT",EDGE,{"derivedFrom":subQ0}),1.0]])]});}
            var Q33;
            {var subQ1=sQuery(id+"F3.wireOp",EDGE,"E6");var subQ3=sQuery(id+"F3.wireOp",EDGE,"E28");var subQ4=makeQuery(id+"F3.imprint","INTERSECT",VERTEX,{"derivedFrom":[subQ1,subQ3]});Q33=makeQuery(id+"F3.imprint","IMPRINT",FACE,{"disambiguationData":[TD([[makeQuery(id+"F3.imprint","IMPRINT",EDGE,{"disambiguationData":[TD([[subQ4,1.0]])],"derivedFrom":subQ3}),1.0]])]});}
            var Q34;
            {var subQ0=sQuery(id+"F3.wireOp",EDGE,"E35");Q34=makeQuery(id+"F3.imprint","IMPRINT",FACE,{"disambiguationData":[TD([[makeQuery(id+"F3.imprint","IMPRINT",EDGE,{"derivedFrom":subQ0}),1.0]])]});}
            var Q35;
            {var subQ1=sQuery(id+"F3.wireOp",EDGE,"E1");var subQ3=sQuery(id+"F3.wireOp",EDGE,"E30");var subQ4=makeQuery(id+"F3.imprint","INTERSECT",VERTEX,{"derivedFrom":[subQ1,subQ3]});Q35=makeQuery(id+"F3.imprint","IMPRINT",FACE,{"disambiguationData":[TD([[makeQuery(id+"F3.imprint","IMPRINT",EDGE,{"disambiguationData":[TD([[subQ4,-1.0]])],"derivedFrom":subQ3}),1.0]])]});}
            var Q36;
            {var subQ1=sQuery(id+"F3.wireOp",EDGE,"E1");var subQ3=sQuery(id+"F3.wireOp",EDGE,"E31");var subQ4=makeQuery(id+"F3.imprint","INTERSECT",VERTEX,{"derivedFrom":[subQ1,subQ3]});Q36=makeQuery(id+"F3.imprint","IMPRINT",FACE,{"disambiguationData":[TD([[makeQuery(id+"F3.imprint","IMPRINT",EDGE,{"disambiguationData":[TD([[subQ4,1.0]])],"derivedFrom":subQ3}),1.0]])]});}
            var Q37;
            {var subQ1=sQuery(id+"F3.wireOp",EDGE,"E2");var subQ3=sQuery(id+"F3.wireOp",EDGE,"E29");var subQ4=makeQuery(id+"F3.imprint","INTERSECT",VERTEX,{"derivedFrom":[subQ1,subQ3]});Q37=makeQuery(id+"F3.imprint","IMPRINT",FACE,{"disambiguationData":[TD([[makeQuery(id+"F3.imprint","IMPRINT",EDGE,{"disambiguationData":[TD([[subQ4,1.0]])],"derivedFrom":subQ3}),1.0]])]});}
            var Q38;
            {var subQ1=sQuery(id+"F3.wireOp",EDGE,"E2");var subQ3=sQuery(id+"F3.wireOp",EDGE,"E29");var subQ4=makeQuery(id+"F3.imprint","INTERSECT",VERTEX,{"derivedFrom":[subQ1,subQ3]});Q38=makeQuery(id+"F3.imprint","IMPRINT",FACE,{"disambiguationData":[TD([[makeQuery(id+"F3.imprint","IMPRINT",EDGE,{"disambiguationData":[TD([[subQ4,1.0]])],"derivedFrom":subQ1}),1.0]])]});}
            var Q39;
            {var subQ0=sQuery(id+"F3.wireOp",EDGE,"E34");Q39=makeQuery(id+"F3.imprint","IMPRINT",FACE,{"disambiguationData":[TD([[makeQuery(id+"F3.imprint","IMPRINT",EDGE,{"derivedFrom":subQ0}),-1.0]])]});}
            var Q40;
            {var subQ1=sQuery(id+"F3.wireOp",EDGE,"E1");var subQ3=sQuery(id+"F3.wireOp",EDGE,"E33");var subQ4=makeQuery(id+"F3.imprint","INTERSECT",VERTEX,{"derivedFrom":[subQ1,subQ3]});Q40=makeQuery(id+"F3.imprint","IMPRINT",FACE,{"disambiguationData":[TD([[makeQuery(id+"F3.imprint","IMPRINT",EDGE,{"disambiguationData":[TD([[subQ4,1.0]])],"derivedFrom":subQ3}),1.0]])]});}
            var Q41;
            {var subQ1=sQuery(id+"F3.wireOp",EDGE,"E1");var subQ3=sQuery(id+"F3.wireOp",EDGE,"E32");var subQ4=makeQuery(id+"F3.imprint","INTERSECT",VERTEX,{"derivedFrom":[subQ1,subQ3]});Q41=makeQuery(id+"F3.imprint","IMPRINT",FACE,{"disambiguationData":[TD([[makeQuery(id+"F3.imprint","IMPRINT",EDGE,{"disambiguationData":[TD([[subQ4,-1.0]])],"derivedFrom":subQ3}),1.0]])]});}
            var Q42;
            {var subQ1=sQuery(id+"F3.wireOp",EDGE,"E20");Q42=makeQuery(id+"F3.imprint","IMPRINT",FACE,{"disambiguationData":[TD([[makeQuery(id+"F3.imprint","IMPRINT",EDGE,{"derivedFrom":subQ1}),-1.0]])]});}
            var Q43;
            {var subQ0=sQuery(id+"F3.wireOp",EDGE,"E22");Q43=makeQuery(id+"F3.imprint","IMPRINT",FACE,{"disambiguationData":[TD([[makeQuery(id+"F3.imprint","IMPRINT",EDGE,{"derivedFrom":subQ0}),1.0]])]});}
            var Q44;
            {var subQ1=sQuery(id+"F3.wireOp",EDGE,"E2");var subQ3=sQuery(id+"F3.wireOp",EDGE,"E42");var subQ4=makeQuery(id+"F3.imprint","INTERSECT",VERTEX,{"derivedFrom":[subQ1,subQ3]});Q44=makeQuery(id+"F3.imprint","IMPRINT",FACE,{"disambiguationData":[TD([[makeQuery(id+"F3.imprint","IMPRINT",EDGE,{"disambiguationData":[TD([[subQ4,-1.0]])],"derivedFrom":subQ3}),1.0]])]});}
            var Q45;
            {var subQ1=sQuery(id+"F3.wireOp",EDGE,"E5");var subQ3=sQuery(id+"F3.wireOp",EDGE,"E42");var subQ4=makeQuery(id+"F3.imprint","INTERSECT",VERTEX,{"derivedFrom":[subQ1,subQ3]});Q45=makeQuery(id+"F3.imprint","IMPRINT",FACE,{"disambiguationData":[TD([[makeQuery(id+"F3.imprint","IMPRINT",EDGE,{"disambiguationData":[TD([[subQ4,1.0]])],"derivedFrom":subQ3}),1.0]])]});}
            extrude(context, id + "F9", {"entities" : qUnion([Q0, Q1, Q2, Q3, Q4, Q5, Q6, Q7, Q8, Q9, Q10, Q11, Q12, Q13, Q14, Q15, Q16, Q17, Q18, Q19, Q20, Q21, Q22, Q23, Q24, Q25, Q26, Q27, Q28, Q29, Q30, Q31, Q32, Q33, Q34, Q35, Q36, Q37, Q38, Q39, Q40, Q41, Q42, Q43, Q44, Q45]), "depth" : (getVariable(context, 'pin_platform_thickness') + getVariable(context, 'pin_hole_depth')) * mm, "offsetDistance" : 25 * mm});
        }
        {
            var Q0;
            Q0=makeQuery(id+"F4.opExtrude","SWEPT_BODY",BODY,{"disambiguationData":[OSD([sQuery(id+"F3.wireOp",EDGE,"E2"),sQuery(id+"F3.wireOp",EDGE,"E5"),sQuery(id+"F3.wireOp",EDGE,"E42")])]});
            var Q1;
            Q1=makeQuery(id+"F9.opExtrude","SWEPT_BODY",BODY,{"disambiguationData":[OSD([sQuery(id+"F3.wireOp",EDGE,"E2"),sQuery(id+"F3.wireOp",EDGE,"E5"),sQuery(id+"F3.wireOp",EDGE,"E42")])]});
            deleteBodies(context, id + "F10", {"entities" : qUnion([Q0, Q1])});
        }
        {
            var Q0;
            {var subQ0=sQuery(id+"F3.wireOp",EDGE,"E31");var subQ1=sQuery(id+"F3.wireOp",EDGE,"E1");var subQ2=makeQuery(id+"F3.imprint","INTERSECT",VERTEX,{"derivedFrom":[subQ1,subQ0]});Q0=makeQuery(id+"F3.imprint","IMPRINT",FACE,{"disambiguationData":[TD([[makeQuery(id+"F3.imprint","IMPRINT",EDGE,{"disambiguationData":[TD([[subQ2,-1.0]])],"derivedFrom":subQ1}),-1.0]])]});}
            var Q1;
            {var subQ0=sQuery(id+"F3.wireOp",EDGE,"E36");Q1=makeQuery(id+"F3.imprint","IMPRINT",FACE,{"disambiguationData":[TD([[makeQuery(id+"F3.imprint","IMPRINT",EDGE,{"derivedFrom":subQ0}),1.0]])]});}
            var Q2;
            {var subQ0=sQuery(id+"F3.wireOp",EDGE,"E23");var subQ1=sQuery(id+"F3.wireOp",EDGE,"E1");var subQ2=makeQuery(id+"F3.imprint","INTERSECT",VERTEX,{"derivedFrom":[subQ1,subQ0]});Q2=makeQuery(id+"F3.imprint","IMPRINT",FACE,{"disambiguationData":[TD([[makeQuery(id+"F3.imprint","IMPRINT",EDGE,{"disambiguationData":[TD([[subQ2,-1.0]])],"derivedFrom":subQ1}),-1.0]])]});}
            var Q3;
            {var subQ3=sQuery(id+"F3.wireOp",EDGE,"E21");var subQ5=sQuery(id+"F3.wireOp",EDGE,"E37");var subQ6=makeQuery(id+"F3.imprint","INTERSECT",VERTEX,{"derivedFrom":[subQ3,subQ5]});Q3=makeQuery(id+"F3.imprint","IMPRINT",FACE,{"disambiguationData":[TD([[makeQuery(id+"F3.imprint","IMPRINT",EDGE,{"disambiguationData":[TD([[subQ6,1.0]])],"derivedFrom":subQ3}),1.0]])]});}
            var Q4;
            {var subQ3=sQuery(id+"F3.wireOp",EDGE,"E23");var subQ5=sQuery(id+"F3.wireOp",EDGE,"E37");var subQ7=makeQuery(id+"F3.imprint","INTERSECT",VERTEX,{"derivedFrom":[subQ3,subQ5]});Q4=makeQuery(id+"F3.imprint","IMPRINT",FACE,{"disambiguationData":[TD([[makeQuery(id+"F3.imprint","IMPRINT",EDGE,{"disambiguationData":[TD([[subQ7,1.0]])],"derivedFrom":subQ3}),-1.0]])]});}
            var Q5;
            {var subQ1=sQuery(id+"F3.wireOp",EDGE,"E1");var subQ3=sQuery(id+"F3.wireOp",EDGE,"E30");var subQ4=makeQuery(id+"F3.imprint","INTERSECT",VERTEX,{"derivedFrom":[subQ1,subQ3]});Q5=makeQuery(id+"F3.imprint","IMPRINT",FACE,{"disambiguationData":[TD([[makeQuery(id+"F3.imprint","IMPRINT",EDGE,{"disambiguationData":[TD([[subQ4,-1.0]])],"derivedFrom":subQ3}),1.0]])]});}
            var Q6;
            {var subQ1=sQuery(id+"F3.wireOp",EDGE,"E1");var subQ3=sQuery(id+"F3.wireOp",EDGE,"E31");var subQ4=makeQuery(id+"F3.imprint","INTERSECT",VERTEX,{"derivedFrom":[subQ1,subQ3]});Q6=makeQuery(id+"F3.imprint","IMPRINT",FACE,{"disambiguationData":[TD([[makeQuery(id+"F3.imprint","IMPRINT",EDGE,{"disambiguationData":[TD([[subQ4,1.0]])],"derivedFrom":subQ3}),1.0]])]});}
            var Q7;
            {var subQ0=sQuery(id+"F3.wireOp",EDGE,"E34");Q7=makeQuery(id+"F3.imprint","IMPRINT",FACE,{"disambiguationData":[TD([[makeQuery(id+"F3.imprint","IMPRINT",EDGE,{"derivedFrom":subQ0}),-1.0]])]});}
            var Q8;
            {var subQ1=sQuery(id+"F3.wireOp",EDGE,"E1");var subQ7=sQuery(id+"F3.wireOp",EDGE,"E33");var subQ8=makeQuery(id+"F3.imprint","INTERSECT",VERTEX,{"derivedFrom":[subQ1,subQ7]});Q8=makeQuery(id+"F3.imprint","IMPRINT",FACE,{"disambiguationData":[TD([[makeQuery(id+"F3.imprint","IMPRINT",EDGE,{"disambiguationData":[TD([[subQ8,-1.0]])],"derivedFrom":subQ1}),-1.0]])]});}
            var Q9;
            {var subQ1=sQuery(id+"F3.wireOp",EDGE,"E1");var subQ7=sQuery(id+"F3.wireOp",EDGE,"E27");var subQ9=makeQuery(id+"F3.imprint","INTERSECT",VERTEX,{"derivedFrom":[subQ1,subQ7]});Q9=makeQuery(id+"F3.imprint","IMPRINT",FACE,{"disambiguationData":[TD([[makeQuery(id+"F3.imprint","IMPRINT",EDGE,{"disambiguationData":[TD([[subQ9,-1.0]])],"derivedFrom":subQ1}),-1.0]])]});}
            var Q10;
            {var subQ1=sQuery(id+"F3.wireOp",EDGE,"E1");var subQ3=sQuery(id+"F3.wireOp",EDGE,"E23");var subQ4=makeQuery(id+"F3.imprint","INTERSECT",VERTEX,{"derivedFrom":[subQ1,subQ3]});Q10=makeQuery(id+"F3.imprint","IMPRINT",FACE,{"disambiguationData":[TD([[makeQuery(id+"F3.imprint","IMPRINT",EDGE,{"disambiguationData":[TD([[subQ4,-1.0]])],"derivedFrom":subQ3}),-1.0]])]});}
            var Q11;
            {var subQ1=sQuery(id+"F3.wireOp",EDGE,"E1");var subQ3=sQuery(id+"F3.wireOp",EDGE,"E21");var subQ4=makeQuery(id+"F3.imprint","INTERSECT",VERTEX,{"derivedFrom":[subQ1,subQ3]});Q11=makeQuery(id+"F3.imprint","IMPRINT",FACE,{"disambiguationData":[TD([[makeQuery(id+"F3.imprint","IMPRINT",EDGE,{"disambiguationData":[TD([[subQ4,-1.0]])],"derivedFrom":subQ3}),1.0]])]});}
            var Q12;
            {var subQ1=sQuery(id+"F3.wireOp",EDGE,"E1");var subQ3=sQuery(id+"F3.wireOp",EDGE,"E27");var subQ4=makeQuery(id+"F3.imprint","INTERSECT",VERTEX,{"derivedFrom":[subQ1,subQ3]});Q12=makeQuery(id+"F3.imprint","IMPRINT",FACE,{"disambiguationData":[TD([[makeQuery(id+"F3.imprint","IMPRINT",EDGE,{"disambiguationData":[TD([[subQ4,1.0]])],"derivedFrom":subQ3}),1.0]])]});}
            var Q13;
            {var subQ1=sQuery(id+"F3.wireOp",EDGE,"E1");var subQ3=sQuery(id+"F3.wireOp",EDGE,"E26");var subQ4=makeQuery(id+"F3.imprint","INTERSECT",VERTEX,{"derivedFrom":[subQ1,subQ3]});Q13=makeQuery(id+"F3.imprint","IMPRINT",FACE,{"disambiguationData":[TD([[makeQuery(id+"F3.imprint","IMPRINT",EDGE,{"disambiguationData":[TD([[subQ4,-1.0]])],"derivedFrom":subQ3}),1.0]])]});}
            var Q14;
            {var subQ1=sQuery(id+"F3.wireOp",EDGE,"E1");var subQ3=sQuery(id+"F3.wireOp",EDGE,"E32");var subQ4=makeQuery(id+"F3.imprint","INTERSECT",VERTEX,{"derivedFrom":[subQ1,subQ3]});Q14=makeQuery(id+"F3.imprint","IMPRINT",FACE,{"disambiguationData":[TD([[makeQuery(id+"F3.imprint","IMPRINT",EDGE,{"disambiguationData":[TD([[subQ4,-1.0]])],"derivedFrom":subQ3}),1.0]])]});}
            var Q15;
            {var subQ1=sQuery(id+"F3.wireOp",EDGE,"E1");var subQ3=sQuery(id+"F3.wireOp",EDGE,"E33");var subQ4=makeQuery(id+"F3.imprint","INTERSECT",VERTEX,{"derivedFrom":[subQ1,subQ3]});Q15=makeQuery(id+"F3.imprint","IMPRINT",FACE,{"disambiguationData":[TD([[makeQuery(id+"F3.imprint","IMPRINT",EDGE,{"disambiguationData":[TD([[subQ4,1.0]])],"derivedFrom":subQ3}),1.0]])]});}
            var Q16;
            {var subQ0=sQuery(id+"F3.wireOp",EDGE,"E23");var subQ1=sQuery(id+"F3.wireOp",EDGE,"E1");var subQ2=makeQuery(id+"F3.imprint","INTERSECT",VERTEX,{"derivedFrom":[subQ1,subQ0]});Q16=makeQuery(id+"F3.imprint","IMPRINT",FACE,{"disambiguationData":[TD([[makeQuery(id+"F3.imprint","IMPRINT",EDGE,{"disambiguationData":[TD([[subQ2,-1.0]])],"derivedFrom":subQ1}),1.0]])]});}
            var Q17;
            {var subQ1=sQuery(id+"F3.wireOp",EDGE,"E1");var subQ3=sQuery(id+"F3.wireOp",EDGE,"E23");var subQ4=makeQuery(id+"F3.imprint","INTERSECT",VERTEX,{"derivedFrom":[subQ1,subQ3]});Q17=makeQuery(id+"F3.imprint","IMPRINT",FACE,{"disambiguationData":[TD([[makeQuery(id+"F3.imprint","IMPRINT",EDGE,{"disambiguationData":[TD([[subQ4,1.0]])],"derivedFrom":subQ3}),-1.0]])]});}
            var Q18;
            {var subQ1=sQuery(id+"F3.wireOp",EDGE,"E1");var subQ3=sQuery(id+"F3.wireOp",EDGE,"E21");var subQ4=makeQuery(id+"F3.imprint","INTERSECT",VERTEX,{"derivedFrom":[subQ1,subQ3]});Q18=makeQuery(id+"F3.imprint","IMPRINT",FACE,{"disambiguationData":[TD([[makeQuery(id+"F3.imprint","IMPRINT",EDGE,{"disambiguationData":[TD([[subQ4,1.0]])],"derivedFrom":subQ3}),1.0]])]});}
            var Q19;
            {var subQ0=sQuery(id+"F3.wireOp",EDGE,"E4");Q19=makeQuery(id+"F3.imprint","IMPRINT",FACE,{"disambiguationData":[TD([[makeQuery(id+"F3.imprint","IMPRINT",EDGE,{"derivedFrom":subQ0}),-1.0]])]});}
            var Q20;
            {var subQ0=sQuery(id+"F3.wireOp",EDGE,"E27");var subQ1=sQuery(id+"F3.wireOp",EDGE,"E1");var subQ2=makeQuery(id+"F3.imprint","INTERSECT",VERTEX,{"derivedFrom":[subQ1,subQ0]});Q20=makeQuery(id+"F3.imprint","IMPRINT",FACE,{"disambiguationData":[TD([[makeQuery(id+"F3.imprint","IMPRINT",EDGE,{"disambiguationData":[TD([[subQ2,-1.0]])],"derivedFrom":subQ1}),1.0]])]});}
            var Q21;
            {var subQ0=sQuery(id+"F3.wireOp",EDGE,"E4");Q21=makeQuery(id+"F3.imprint","IMPRINT",FACE,{"disambiguationData":[TD([[makeQuery(id+"F3.imprint","IMPRINT",EDGE,{"derivedFrom":subQ0}),1.0]])]});}
            var Q22;
            {var subQ1=sQuery(id+"F3.wireOp",EDGE,"E2");var subQ3=sQuery(id+"F3.wireOp",EDGE,"E29");var subQ4=makeQuery(id+"F3.imprint","INTERSECT",VERTEX,{"derivedFrom":[subQ1,subQ3]});Q22=makeQuery(id+"F3.imprint","IMPRINT",FACE,{"disambiguationData":[TD([[makeQuery(id+"F3.imprint","IMPRINT",EDGE,{"disambiguationData":[TD([[subQ4,-1.0]])],"derivedFrom":subQ3}),1.0]])]});}
            var Q23;
            {var subQ0=sQuery(id+"F3.wireOp",EDGE,"E22");Q23=makeQuery(id+"F3.imprint","IMPRINT",FACE,{"disambiguationData":[TD([[makeQuery(id+"F3.imprint","IMPRINT",EDGE,{"derivedFrom":subQ0}),1.0]])]});}
            var Q24;
            {var subQ1=sQuery(id+"F3.wireOp",EDGE,"E20");Q24=makeQuery(id+"F3.imprint","IMPRINT",FACE,{"disambiguationData":[TD([[makeQuery(id+"F3.imprint","IMPRINT",EDGE,{"derivedFrom":subQ1}),-1.0]])]});}
            var Q25;
            {var subQ1=sQuery(id+"F3.wireOp",EDGE,"E1");var subQ3=sQuery(id+"F3.wireOp",EDGE,"E30");var subQ4=makeQuery(id+"F3.imprint","INTERSECT",VERTEX,{"derivedFrom":[subQ1,subQ3]});Q25=makeQuery(id+"F3.imprint","IMPRINT",FACE,{"disambiguationData":[TD([[makeQuery(id+"F3.imprint","IMPRINT",EDGE,{"disambiguationData":[TD([[subQ4,1.0]])],"derivedFrom":subQ3}),1.0]])]});}
            var Q26;
            {var subQ1=sQuery(id+"F3.wireOp",EDGE,"E1");var subQ3=sQuery(id+"F3.wireOp",EDGE,"E27");var subQ4=makeQuery(id+"F3.imprint","INTERSECT",VERTEX,{"derivedFrom":[subQ1,subQ3]});Q26=makeQuery(id+"F3.imprint","IMPRINT",FACE,{"disambiguationData":[TD([[makeQuery(id+"F3.imprint","IMPRINT",EDGE,{"disambiguationData":[TD([[subQ4,-1.0]])],"derivedFrom":subQ3}),1.0]])]});}
            var Q27;
            {var subQ1=sQuery(id+"F3.wireOp",EDGE,"E1");var subQ3=sQuery(id+"F3.wireOp",EDGE,"E26");var subQ4=makeQuery(id+"F3.imprint","INTERSECT",VERTEX,{"derivedFrom":[subQ1,subQ3]});Q27=makeQuery(id+"F3.imprint","IMPRINT",FACE,{"disambiguationData":[TD([[makeQuery(id+"F3.imprint","IMPRINT",EDGE,{"disambiguationData":[TD([[subQ4,1.0]])],"derivedFrom":subQ3}),1.0]])]});}
            var Q28;
            {var subQ3=sQuery(id+"F3.wireOp",EDGE,"E25");Q28=makeQuery(id+"F3.imprint","IMPRINT",FACE,{"disambiguationData":[TD([[makeQuery(id+"F3.imprint","IMPRINT",EDGE,{"derivedFrom":subQ3}),1.0]])]});}
            var Q29;
            {var subQ3=sQuery(id+"F3.wireOp",EDGE,"E24");Q29=makeQuery(id+"F3.imprint","IMPRINT",FACE,{"disambiguationData":[TD([[makeQuery(id+"F3.imprint","IMPRINT",EDGE,{"derivedFrom":subQ3}),1.0]])]});}
            var Q30;
            {var subQ0=sQuery(id+"F3.wireOp",EDGE,"E33");var subQ1=sQuery(id+"F3.wireOp",EDGE,"E1");var subQ2=makeQuery(id+"F3.imprint","INTERSECT",VERTEX,{"derivedFrom":[subQ1,subQ0]});Q30=makeQuery(id+"F3.imprint","IMPRINT",FACE,{"disambiguationData":[TD([[makeQuery(id+"F3.imprint","IMPRINT",EDGE,{"disambiguationData":[TD([[subQ2,-1.0]])],"derivedFrom":subQ1}),1.0]])]});}
            var Q31;
            {var subQ1=sQuery(id+"F3.wireOp",EDGE,"E1");var subQ3=sQuery(id+"F3.wireOp",EDGE,"E33");var subQ4=makeQuery(id+"F3.imprint","INTERSECT",VERTEX,{"derivedFrom":[subQ1,subQ3]});Q31=makeQuery(id+"F3.imprint","IMPRINT",FACE,{"disambiguationData":[TD([[makeQuery(id+"F3.imprint","IMPRINT",EDGE,{"disambiguationData":[TD([[subQ4,-1.0]])],"derivedFrom":subQ3}),1.0]])]});}
            var Q32;
            {var subQ1=sQuery(id+"F3.wireOp",EDGE,"E6");var subQ3=sQuery(id+"F3.wireOp",EDGE,"E28");var subQ4=makeQuery(id+"F3.imprint","INTERSECT",VERTEX,{"derivedFrom":[subQ1,subQ3]});Q32=makeQuery(id+"F3.imprint","IMPRINT",FACE,{"disambiguationData":[TD([[makeQuery(id+"F3.imprint","IMPRINT",EDGE,{"disambiguationData":[TD([[subQ4,1.0]])],"derivedFrom":subQ3}),1.0]])]});}
            var Q33;
            {var subQ1=sQuery(id+"F3.wireOp",EDGE,"E6");var subQ3=sQuery(id+"F3.wireOp",EDGE,"E28");var subQ4=makeQuery(id+"F3.imprint","INTERSECT",VERTEX,{"derivedFrom":[subQ1,subQ3]});Q33=makeQuery(id+"F3.imprint","IMPRINT",FACE,{"disambiguationData":[TD([[makeQuery(id+"F3.imprint","IMPRINT",EDGE,{"disambiguationData":[TD([[subQ4,-1.0]])],"derivedFrom":subQ3}),1.0]])]});}
            var Q34;
            {var subQ1=sQuery(id+"F3.wireOp",EDGE,"E1");var subQ3=sQuery(id+"F3.wireOp",EDGE,"E32");var subQ4=makeQuery(id+"F3.imprint","INTERSECT",VERTEX,{"derivedFrom":[subQ1,subQ3]});Q34=makeQuery(id+"F3.imprint","IMPRINT",FACE,{"disambiguationData":[TD([[makeQuery(id+"F3.imprint","IMPRINT",EDGE,{"disambiguationData":[TD([[subQ4,1.0]])],"derivedFrom":subQ3}),1.0]])]});}
            var Q35;
            {var subQ5=sQuery(id+"F3.wireOp",EDGE,"E2");var subQ7=sQuery(id+"F3.wireOp",EDGE,"E42");var subQ8=makeQuery(id+"F3.imprint","INTERSECT",VERTEX,{"derivedFrom":[subQ5,subQ7]});Q35=makeQuery(id+"F3.imprint","IMPRINT",FACE,{"disambiguationData":[TD([[makeQuery(id+"F3.imprint","IMPRINT",EDGE,{"disambiguationData":[TD([[subQ8,-1.0]])],"derivedFrom":subQ5}),1.0]])]});}
            var Q36;
            {var subQ1=sQuery(id+"F3.wireOp",EDGE,"E25");Q36=makeQuery(id+"F3.imprint","IMPRINT",FACE,{"disambiguationData":[TD([[makeQuery(id+"F3.imprint","IMPRINT",EDGE,{"derivedFrom":subQ1}),-1.0]])]});}
            var Q37;
            {var subQ1=sQuery(id+"F3.wireOp",EDGE,"E2");var subQ3=sQuery(id+"F3.wireOp",EDGE,"E29");var subQ4=makeQuery(id+"F3.imprint","INTERSECT",VERTEX,{"derivedFrom":[subQ1,subQ3]});Q37=makeQuery(id+"F3.imprint","IMPRINT",FACE,{"disambiguationData":[TD([[makeQuery(id+"F3.imprint","IMPRINT",EDGE,{"disambiguationData":[TD([[subQ4,1.0]])],"derivedFrom":subQ3}),1.0]])]});}
            var Q38;
            {var subQ1=sQuery(id+"F3.wireOp",EDGE,"E1");var subQ3=sQuery(id+"F3.wireOp",EDGE,"E31");var subQ4=makeQuery(id+"F3.imprint","INTERSECT",VERTEX,{"derivedFrom":[subQ1,subQ3]});Q38=makeQuery(id+"F3.imprint","IMPRINT",FACE,{"disambiguationData":[TD([[makeQuery(id+"F3.imprint","IMPRINT",EDGE,{"disambiguationData":[TD([[subQ4,-1.0]])],"derivedFrom":subQ3}),1.0]])]});}
            var Q39;
            {var subQ0=sQuery(id+"F3.wireOp",EDGE,"E31");var subQ1=sQuery(id+"F3.wireOp",EDGE,"E1");var subQ2=makeQuery(id+"F3.imprint","INTERSECT",VERTEX,{"derivedFrom":[subQ1,subQ0]});Q39=makeQuery(id+"F3.imprint","IMPRINT",FACE,{"disambiguationData":[TD([[makeQuery(id+"F3.imprint","IMPRINT",EDGE,{"disambiguationData":[TD([[subQ2,-1.0]])],"derivedFrom":subQ1}),1.0]])]});}
            var Q40;
            {var subQ1=sQuery(id+"F3.wireOp",EDGE,"E2");var subQ3=sQuery(id+"F3.wireOp",EDGE,"E42");var subQ4=makeQuery(id+"F3.imprint","INTERSECT",VERTEX,{"derivedFrom":[subQ1,subQ3]});Q40=makeQuery(id+"F3.imprint","IMPRINT",FACE,{"disambiguationData":[TD([[makeQuery(id+"F3.imprint","IMPRINT",EDGE,{"disambiguationData":[TD([[subQ4,-1.0]])],"derivedFrom":subQ3}),1.0]])]});}
            var Q41;
            {var subQ1=sQuery(id+"F3.wireOp",EDGE,"E5");var subQ3=sQuery(id+"F3.wireOp",EDGE,"E42");var subQ4=makeQuery(id+"F3.imprint","INTERSECT",VERTEX,{"derivedFrom":[subQ1,subQ3]});Q41=makeQuery(id+"F3.imprint","IMPRINT",FACE,{"disambiguationData":[TD([[makeQuery(id+"F3.imprint","IMPRINT",EDGE,{"disambiguationData":[TD([[subQ4,1.0]])],"derivedFrom":subQ3}),1.0]])]});}
            var Q42;
            {var subQ1=sQuery(id+"F3.wireOp",EDGE,"E5");var subQ3=sQuery(id+"F3.wireOp",EDGE,"E42");var subQ4=makeQuery(id+"F3.imprint","INTERSECT",VERTEX,{"derivedFrom":[subQ1,subQ3]});Q42=makeQuery(id+"F3.imprint","IMPRINT",FACE,{"disambiguationData":[TD([[makeQuery(id+"F3.imprint","IMPRINT",EDGE,{"disambiguationData":[TD([[subQ4,-1.0]])],"derivedFrom":subQ3}),1.0]])]});}
            var Q43;
            {var subQ1=sQuery(id+"F3.wireOp",EDGE,"E2");var subQ3=sQuery(id+"F3.wireOp",EDGE,"E42");var subQ4=makeQuery(id+"F3.imprint","INTERSECT",VERTEX,{"derivedFrom":[subQ1,subQ3]});Q43=makeQuery(id+"F3.imprint","IMPRINT",FACE,{"disambiguationData":[TD([[makeQuery(id+"F3.imprint","IMPRINT",EDGE,{"disambiguationData":[TD([[subQ4,1.0]])],"derivedFrom":subQ3}),1.0]])]});}
            extrude(context, id + "F11", {"entities" : qUnion([Q0, Q1, Q2, Q3, Q4, Q5, Q6, Q7, Q8, Q9, Q10, Q11, Q12, Q13, Q14, Q15, Q16, Q17, Q18, Q19, Q20, Q21, Q22, Q23, Q24, Q25, Q26, Q27, Q28, Q29, Q30, Q31, Q32, Q33, Q34, Q35, Q36, Q37, Q38, Q39, Q40, Q41, Q42, Q43]), "depth" : (getVariable(context, 'pin_platform_thickness')) * mm, "offsetDistance" : 25 * mm});
        }
        {
            var Q0;
            Q0=makeQuery(id+"F11.opExtrude","SWEPT_BODY",BODY,{"disambiguationData":[OSD([sQuery(id+"F3.wireOp",EDGE,"E3"),sQuery(id+"F3.wireOp",EDGE,"E11"),sQuery(id+"F3.wireOp",EDGE,"E12"),sQuery(id+"F3.wireOp",EDGE,"E13"),sQuery(id+"F3.wireOp",EDGE,"E14"),sQuery(id+"F3.wireOp",EDGE,"E15"),sQuery(id+"F3.wireOp",EDGE,"E16"),sQuery(id+"F3.wireOp",EDGE,"E17"),sQuery(id+"F3.wireOp",EDGE,"E21"),sQuery(id+"F3.wireOp",EDGE,"E23"),sQuery(id+"F3.wireOp",EDGE,"E26"),sQuery(id+"F3.wireOp",EDGE,"E27"),sQuery(id+"F3.wireOp",EDGE,"E30"),sQuery(id+"F3.wireOp",EDGE,"E31"),sQuery(id+"F3.wireOp",EDGE,"E34"),sQuery(id+"F3.wireOp",EDGE,"E36"),sQuery(id+"F3.wireOp",EDGE,"E37")])]});
            transform(context, id + "F12", {"entities" : qUnion([Q0]), "transformType" : TransformType.TRANSLATION_3D, "dx" : 0 * mm, "dy" : 0 * mm, "dz" : 0 * mm, "makeCopy" : true});
        }
        {
            var Q0;
            {var subQ0=sQuery(id+"F3.wireOp",EDGE,"E23");var subQ1=sQuery(id+"F3.wireOp",EDGE,"E1");var subQ2=makeQuery(id+"F3.imprint","INTERSECT",VERTEX,{"derivedFrom":[subQ1,subQ0]});Q0=makeQuery(id+"F3.imprint","IMPRINT",FACE,{"disambiguationData":[TD([[makeQuery(id+"F3.imprint","IMPRINT",EDGE,{"disambiguationData":[TD([[subQ2,-1.0]])],"derivedFrom":subQ1}),1.0]])]});}
            var Q1;
            {var subQ1=sQuery(id+"F3.wireOp",EDGE,"E1");var subQ3=sQuery(id+"F3.wireOp",EDGE,"E23");var subQ4=makeQuery(id+"F3.imprint","INTERSECT",VERTEX,{"derivedFrom":[subQ1,subQ3]});Q1=makeQuery(id+"F3.imprint","IMPRINT",FACE,{"disambiguationData":[TD([[makeQuery(id+"F3.imprint","IMPRINT",EDGE,{"disambiguationData":[TD([[subQ4,1.0]])],"derivedFrom":subQ3}),-1.0]])]});}
            var Q2;
            {var subQ0=sQuery(id+"F3.wireOp",EDGE,"E4");Q2=makeQuery(id+"F3.imprint","IMPRINT",FACE,{"disambiguationData":[TD([[makeQuery(id+"F3.imprint","IMPRINT",EDGE,{"derivedFrom":subQ0}),1.0]])]});}
            var Q3;
            {var subQ1=sQuery(id+"F3.wireOp",EDGE,"E1");var subQ3=sQuery(id+"F3.wireOp",EDGE,"E21");var subQ4=makeQuery(id+"F3.imprint","INTERSECT",VERTEX,{"derivedFrom":[subQ1,subQ3]});Q3=makeQuery(id+"F3.imprint","IMPRINT",FACE,{"disambiguationData":[TD([[makeQuery(id+"F3.imprint","IMPRINT",EDGE,{"disambiguationData":[TD([[subQ4,1.0]])],"derivedFrom":subQ3}),1.0]])]});}
            var Q4;
            {var subQ0=sQuery(id+"F3.wireOp",EDGE,"E27");var subQ1=sQuery(id+"F3.wireOp",EDGE,"E1");var subQ2=makeQuery(id+"F3.imprint","INTERSECT",VERTEX,{"derivedFrom":[subQ1,subQ0]});Q4=makeQuery(id+"F3.imprint","IMPRINT",FACE,{"disambiguationData":[TD([[makeQuery(id+"F3.imprint","IMPRINT",EDGE,{"disambiguationData":[TD([[subQ2,-1.0]])],"derivedFrom":subQ1}),1.0]])]});}
            var Q5;
            {var subQ0=sQuery(id+"F3.wireOp",EDGE,"E4");Q5=makeQuery(id+"F3.imprint","IMPRINT",FACE,{"disambiguationData":[TD([[makeQuery(id+"F3.imprint","IMPRINT",EDGE,{"derivedFrom":subQ0}),-1.0]])]});}
            var Q6;
            {var subQ1=sQuery(id+"F3.wireOp",EDGE,"E1");var subQ3=sQuery(id+"F3.wireOp",EDGE,"E27");var subQ4=makeQuery(id+"F3.imprint","INTERSECT",VERTEX,{"derivedFrom":[subQ1,subQ3]});Q6=makeQuery(id+"F3.imprint","IMPRINT",FACE,{"disambiguationData":[TD([[makeQuery(id+"F3.imprint","IMPRINT",EDGE,{"disambiguationData":[TD([[subQ4,-1.0]])],"derivedFrom":subQ3}),1.0]])]});}
            var Q7;
            {var subQ3=sQuery(id+"F3.wireOp",EDGE,"E24");Q7=makeQuery(id+"F3.imprint","IMPRINT",FACE,{"disambiguationData":[TD([[makeQuery(id+"F3.imprint","IMPRINT",EDGE,{"derivedFrom":subQ3}),1.0]])]});}
            var Q8;
            {var subQ1=sQuery(id+"F3.wireOp",EDGE,"E20");Q8=makeQuery(id+"F3.imprint","IMPRINT",FACE,{"disambiguationData":[TD([[makeQuery(id+"F3.imprint","IMPRINT",EDGE,{"derivedFrom":subQ1}),-1.0]])]});}
            var Q9;
            {var subQ0=sQuery(id+"F3.wireOp",EDGE,"E22");Q9=makeQuery(id+"F3.imprint","IMPRINT",FACE,{"disambiguationData":[TD([[makeQuery(id+"F3.imprint","IMPRINT",EDGE,{"derivedFrom":subQ0}),1.0]])]});}
            var Q10;
            {var subQ1=sQuery(id+"F3.wireOp",EDGE,"E2");var subQ3=sQuery(id+"F3.wireOp",EDGE,"E29");var subQ4=makeQuery(id+"F3.imprint","INTERSECT",VERTEX,{"derivedFrom":[subQ1,subQ3]});Q10=makeQuery(id+"F3.imprint","IMPRINT",FACE,{"disambiguationData":[TD([[makeQuery(id+"F3.imprint","IMPRINT",EDGE,{"disambiguationData":[TD([[subQ4,-1.0]])],"derivedFrom":subQ3}),1.0]])]});}
            var Q11;
            {var subQ1=sQuery(id+"F3.wireOp",EDGE,"E1");var subQ3=sQuery(id+"F3.wireOp",EDGE,"E30");var subQ4=makeQuery(id+"F3.imprint","INTERSECT",VERTEX,{"derivedFrom":[subQ1,subQ3]});Q11=makeQuery(id+"F3.imprint","IMPRINT",FACE,{"disambiguationData":[TD([[makeQuery(id+"F3.imprint","IMPRINT",EDGE,{"disambiguationData":[TD([[subQ4,1.0]])],"derivedFrom":subQ3}),1.0]])]});}
            var Q12;
            {var subQ1=sQuery(id+"F3.wireOp",EDGE,"E1");var subQ3=sQuery(id+"F3.wireOp",EDGE,"E31");var subQ4=makeQuery(id+"F3.imprint","INTERSECT",VERTEX,{"derivedFrom":[subQ1,subQ3]});Q12=makeQuery(id+"F3.imprint","IMPRINT",FACE,{"disambiguationData":[TD([[makeQuery(id+"F3.imprint","IMPRINT",EDGE,{"disambiguationData":[TD([[subQ4,-1.0]])],"derivedFrom":subQ3}),1.0]])]});}
            var Q13;
            {var subQ5=sQuery(id+"F3.wireOp",EDGE,"E2");var subQ7=sQuery(id+"F3.wireOp",EDGE,"E42");var subQ8=makeQuery(id+"F3.imprint","INTERSECT",VERTEX,{"derivedFrom":[subQ5,subQ7]});Q13=makeQuery(id+"F3.imprint","IMPRINT",FACE,{"disambiguationData":[TD([[makeQuery(id+"F3.imprint","IMPRINT",EDGE,{"disambiguationData":[TD([[subQ8,-1.0]])],"derivedFrom":subQ5}),1.0]])]});}
            var Q14;
            {var subQ1=sQuery(id+"F3.wireOp",EDGE,"E2");var subQ3=sQuery(id+"F3.wireOp",EDGE,"E29");var subQ4=makeQuery(id+"F3.imprint","INTERSECT",VERTEX,{"derivedFrom":[subQ1,subQ3]});Q14=makeQuery(id+"F3.imprint","IMPRINT",FACE,{"disambiguationData":[TD([[makeQuery(id+"F3.imprint","IMPRINT",EDGE,{"disambiguationData":[TD([[subQ4,1.0]])],"derivedFrom":subQ3}),1.0]])]});}
            var Q15;
            {var subQ1=sQuery(id+"F3.wireOp",EDGE,"E2");var subQ3=sQuery(id+"F3.wireOp",EDGE,"E42");var subQ4=makeQuery(id+"F3.imprint","INTERSECT",VERTEX,{"derivedFrom":[subQ1,subQ3]});Q15=makeQuery(id+"F3.imprint","IMPRINT",FACE,{"disambiguationData":[TD([[makeQuery(id+"F3.imprint","IMPRINT",EDGE,{"disambiguationData":[TD([[subQ4,1.0]])],"derivedFrom":subQ3}),1.0]])]});}
            var Q16;
            {var subQ1=sQuery(id+"F3.wireOp",EDGE,"E5");var subQ3=sQuery(id+"F3.wireOp",EDGE,"E42");var subQ4=makeQuery(id+"F3.imprint","INTERSECT",VERTEX,{"derivedFrom":[subQ1,subQ3]});Q16=makeQuery(id+"F3.imprint","IMPRINT",FACE,{"disambiguationData":[TD([[makeQuery(id+"F3.imprint","IMPRINT",EDGE,{"disambiguationData":[TD([[subQ4,-1.0]])],"derivedFrom":subQ3}),1.0]])]});}
            var Q17;
            {var subQ1=sQuery(id+"F3.wireOp",EDGE,"E5");var subQ3=sQuery(id+"F3.wireOp",EDGE,"E42");var subQ4=makeQuery(id+"F3.imprint","INTERSECT",VERTEX,{"derivedFrom":[subQ1,subQ3]});Q17=makeQuery(id+"F3.imprint","IMPRINT",FACE,{"disambiguationData":[TD([[makeQuery(id+"F3.imprint","IMPRINT",EDGE,{"disambiguationData":[TD([[subQ4,1.0]])],"derivedFrom":subQ3}),1.0]])]});}
            var Q18;
            {var subQ1=sQuery(id+"F3.wireOp",EDGE,"E2");var subQ3=sQuery(id+"F3.wireOp",EDGE,"E42");var subQ4=makeQuery(id+"F3.imprint","INTERSECT",VERTEX,{"derivedFrom":[subQ1,subQ3]});Q18=makeQuery(id+"F3.imprint","IMPRINT",FACE,{"disambiguationData":[TD([[makeQuery(id+"F3.imprint","IMPRINT",EDGE,{"disambiguationData":[TD([[subQ4,-1.0]])],"derivedFrom":subQ3}),1.0]])]});}
            var Q19;
            {var subQ1=sQuery(id+"F3.wireOp",EDGE,"E25");Q19=makeQuery(id+"F3.imprint","IMPRINT",FACE,{"disambiguationData":[TD([[makeQuery(id+"F3.imprint","IMPRINT",EDGE,{"derivedFrom":subQ1}),-1.0]])]});}
            var Q20;
            {var subQ3=sQuery(id+"F3.wireOp",EDGE,"E25");Q20=makeQuery(id+"F3.imprint","IMPRINT",FACE,{"disambiguationData":[TD([[makeQuery(id+"F3.imprint","IMPRINT",EDGE,{"derivedFrom":subQ3}),1.0]])]});}
            var Q21;
            {var subQ1=sQuery(id+"F3.wireOp",EDGE,"E6");var subQ3=sQuery(id+"F3.wireOp",EDGE,"E28");var subQ4=makeQuery(id+"F3.imprint","INTERSECT",VERTEX,{"derivedFrom":[subQ1,subQ3]});Q21=makeQuery(id+"F3.imprint","IMPRINT",FACE,{"disambiguationData":[TD([[makeQuery(id+"F3.imprint","IMPRINT",EDGE,{"disambiguationData":[TD([[subQ4,1.0]])],"derivedFrom":subQ3}),1.0]])]});}
            var Q22;
            {var subQ1=sQuery(id+"F3.wireOp",EDGE,"E6");var subQ3=sQuery(id+"F3.wireOp",EDGE,"E28");var subQ4=makeQuery(id+"F3.imprint","INTERSECT",VERTEX,{"derivedFrom":[subQ1,subQ3]});Q22=makeQuery(id+"F3.imprint","IMPRINT",FACE,{"disambiguationData":[TD([[makeQuery(id+"F3.imprint","IMPRINT",EDGE,{"disambiguationData":[TD([[subQ4,-1.0]])],"derivedFrom":subQ3}),1.0]])]});}
            var Q23;
            {var subQ1=sQuery(id+"F3.wireOp",EDGE,"E1");var subQ3=sQuery(id+"F3.wireOp",EDGE,"E26");var subQ4=makeQuery(id+"F3.imprint","INTERSECT",VERTEX,{"derivedFrom":[subQ1,subQ3]});Q23=makeQuery(id+"F3.imprint","IMPRINT",FACE,{"disambiguationData":[TD([[makeQuery(id+"F3.imprint","IMPRINT",EDGE,{"disambiguationData":[TD([[subQ4,1.0]])],"derivedFrom":subQ3}),1.0]])]});}
            var Q24;
            {var subQ0=sQuery(id+"F3.wireOp",EDGE,"E33");var subQ1=sQuery(id+"F3.wireOp",EDGE,"E1");var subQ2=makeQuery(id+"F3.imprint","INTERSECT",VERTEX,{"derivedFrom":[subQ1,subQ0]});Q24=makeQuery(id+"F3.imprint","IMPRINT",FACE,{"disambiguationData":[TD([[makeQuery(id+"F3.imprint","IMPRINT",EDGE,{"disambiguationData":[TD([[subQ2,-1.0]])],"derivedFrom":subQ1}),1.0]])]});}
            var Q25;
            {var subQ1=sQuery(id+"F3.wireOp",EDGE,"E1");var subQ3=sQuery(id+"F3.wireOp",EDGE,"E32");var subQ4=makeQuery(id+"F3.imprint","INTERSECT",VERTEX,{"derivedFrom":[subQ1,subQ3]});Q25=makeQuery(id+"F3.imprint","IMPRINT",FACE,{"disambiguationData":[TD([[makeQuery(id+"F3.imprint","IMPRINT",EDGE,{"disambiguationData":[TD([[subQ4,1.0]])],"derivedFrom":subQ3}),1.0]])]});}
            var Q26;
            {var subQ1=sQuery(id+"F3.wireOp",EDGE,"E1");var subQ3=sQuery(id+"F3.wireOp",EDGE,"E33");var subQ4=makeQuery(id+"F3.imprint","INTERSECT",VERTEX,{"derivedFrom":[subQ1,subQ3]});Q26=makeQuery(id+"F3.imprint","IMPRINT",FACE,{"disambiguationData":[TD([[makeQuery(id+"F3.imprint","IMPRINT",EDGE,{"disambiguationData":[TD([[subQ4,-1.0]])],"derivedFrom":subQ3}),1.0]])]});}
            var Q27;
            {var subQ0=sQuery(id+"F3.wireOp",EDGE,"E31");var subQ1=sQuery(id+"F3.wireOp",EDGE,"E1");var subQ2=makeQuery(id+"F3.imprint","INTERSECT",VERTEX,{"derivedFrom":[subQ1,subQ0]});Q27=makeQuery(id+"F3.imprint","IMPRINT",FACE,{"disambiguationData":[TD([[makeQuery(id+"F3.imprint","IMPRINT",EDGE,{"disambiguationData":[TD([[subQ2,-1.0]])],"derivedFrom":subQ1}),1.0]])]});}
            extrude(context, id + "F13", {"entities" : qUnion([Q0, Q1, Q2, Q3, Q4, Q5, Q6, Q7, Q8, Q9, Q10, Q11, Q12, Q13, Q14, Q15, Q16, Q17, Q18, Q19, Q20, Q21, Q22, Q23, Q24, Q25, Q26, Q27]), "depth" : (getVariable(context, 'pin_platform_thickness') + getVariable(context, 'pin_shaft_height')) * mm, "offsetDistance" : 25 * mm});
        }
        {
            var Q0;
            Q0=makeQuery(id+"F12.opPattern","COPY",BODY,{"derivedFrom":makeQuery(id+"F11.opExtrude","SWEPT_BODY",BODY,{"disambiguationData":[OSD([sQuery(id+"F3.wireOp",EDGE,"E3"),sQuery(id+"F3.wireOp",EDGE,"E11"),sQuery(id+"F3.wireOp",EDGE,"E12"),sQuery(id+"F3.wireOp",EDGE,"E13"),sQuery(id+"F3.wireOp",EDGE,"E14"),sQuery(id+"F3.wireOp",EDGE,"E15"),sQuery(id+"F3.wireOp",EDGE,"E16"),sQuery(id+"F3.wireOp",EDGE,"E17"),sQuery(id+"F3.wireOp",EDGE,"E21"),sQuery(id+"F3.wireOp",EDGE,"E23"),sQuery(id+"F3.wireOp",EDGE,"E26"),sQuery(id+"F3.wireOp",EDGE,"E27"),sQuery(id+"F3.wireOp",EDGE,"E30"),sQuery(id+"F3.wireOp",EDGE,"E31"),sQuery(id+"F3.wireOp",EDGE,"E34"),sQuery(id+"F3.wireOp",EDGE,"E36"),sQuery(id+"F3.wireOp",EDGE,"E37")])]}),"instanceName":"1"});
            var Q1;
            Q1=sQuery(id+"F3.wireOp",VERTEX,"E0.middle");
            transform(context, id + "F14", {"entities" : qUnion([Q0]), "transformType" : TransformType.SCALE_UNIFORMLY, "scale" : 1.1, "scalePoint" : qUnion([Q1]), "makeCopy" : true});
        }
        {
            var Q0;
            Q0=makeQuery(id+"F12.opPattern","COPY",BODY,{"derivedFrom":makeQuery(id+"F11.opExtrude","SWEPT_BODY",BODY,{"disambiguationData":[OSD([sQuery(id+"F3.wireOp",EDGE,"E3"),sQuery(id+"F3.wireOp",EDGE,"E11"),sQuery(id+"F3.wireOp",EDGE,"E12"),sQuery(id+"F3.wireOp",EDGE,"E13"),sQuery(id+"F3.wireOp",EDGE,"E14"),sQuery(id+"F3.wireOp",EDGE,"E15"),sQuery(id+"F3.wireOp",EDGE,"E16"),sQuery(id+"F3.wireOp",EDGE,"E17"),sQuery(id+"F3.wireOp",EDGE,"E21"),sQuery(id+"F3.wireOp",EDGE,"E23"),sQuery(id+"F3.wireOp",EDGE,"E26"),sQuery(id+"F3.wireOp",EDGE,"E27"),sQuery(id+"F3.wireOp",EDGE,"E30"),sQuery(id+"F3.wireOp",EDGE,"E31"),sQuery(id+"F3.wireOp",EDGE,"E34"),sQuery(id+"F3.wireOp",EDGE,"E36"),sQuery(id+"F3.wireOp",EDGE,"E37")])]}),"instanceName":"1"});
            var Q1;
            Q1=sQuery(id+"F3.wireOp",VERTEX,"E0.middle");
            transform(context, id + "F15", {"entities" : qUnion([Q0]), "transformType" : TransformType.SCALE_UNIFORMLY, "scale" : 1.05, "scalePoint" : qUnion([Q1]), "makeCopy" : true});
        }
        {
            var Q0;
            Q0=makeQuery(id+"F12.opPattern","COPY",BODY,{"derivedFrom":makeQuery(id+"F11.opExtrude","SWEPT_BODY",BODY,{"disambiguationData":[OSD([sQuery(id+"F3.wireOp",EDGE,"E3"),sQuery(id+"F3.wireOp",EDGE,"E11"),sQuery(id+"F3.wireOp",EDGE,"E12"),sQuery(id+"F3.wireOp",EDGE,"E13"),sQuery(id+"F3.wireOp",EDGE,"E14"),sQuery(id+"F3.wireOp",EDGE,"E15"),sQuery(id+"F3.wireOp",EDGE,"E16"),sQuery(id+"F3.wireOp",EDGE,"E17"),sQuery(id+"F3.wireOp",EDGE,"E21"),sQuery(id+"F3.wireOp",EDGE,"E23"),sQuery(id+"F3.wireOp",EDGE,"E26"),sQuery(id+"F3.wireOp",EDGE,"E27"),sQuery(id+"F3.wireOp",EDGE,"E30"),sQuery(id+"F3.wireOp",EDGE,"E31"),sQuery(id+"F3.wireOp",EDGE,"E34"),sQuery(id+"F3.wireOp",EDGE,"E36"),sQuery(id+"F3.wireOp",EDGE,"E37")])]}),"instanceName":"1"});
            var Q1;
            Q1=sQuery(id+"F3.wireOp",VERTEX,"E0.middle");
            transform(context, id + "F16", {"entities" : qUnion([Q0]), "transformType" : TransformType.SCALE_UNIFORMLY, "scale" : 1.07, "scalePoint" : qUnion([Q1]), "makeCopy" : true});
        }
        {
            var Q0;
            Q0=makeQuery(id+"F9.opExtrude","SWEPT_BODY",BODY,{"disambiguationData":[OSD([sQuery(id+"F3.wireOp",EDGE,"E38"),sQuery(id+"F3.wireOp",EDGE,"E39"),sQuery(id+"F3.wireOp",EDGE,"E40"),sQuery(id+"F3.wireOp",EDGE,"E41")])]});
            transform(context, id + "F17", {"entities" : qUnion([Q0]), "transformType" : TransformType.TRANSLATION_3D, "dx" : 0 * mm, "dy" : 0 * mm, "dz" : 0 * mm, "makeCopy" : true});
        }
        {
            var Q0;
            Q0=makeQuery(id+"F17.opPattern","COPY",BODY,{"derivedFrom":makeQuery(id+"F9.opExtrude","SWEPT_BODY",BODY,{"disambiguationData":[OSD([sQuery(id+"F3.wireOp",EDGE,"E38"),sQuery(id+"F3.wireOp",EDGE,"E39"),sQuery(id+"F3.wireOp",EDGE,"E40"),sQuery(id+"F3.wireOp",EDGE,"E41")])]}),"instanceName":"1"});
            transform(context, id + "F18", {"entities" : qUnion([Q0]), "transformType" : TransformType.TRANSLATION_3D, "dx" : 0 * mm, "dy" : 0 * mm, "dz" : 0 * mm, "makeCopy" : true});
        }
        {
            var Q0;
            Q0=makeQuery(id+"F18.opPattern","COPY",BODY,{"derivedFrom":makeQuery(id+"F17.opPattern","COPY",BODY,{"derivedFrom":makeQuery(id+"F9.opExtrude","SWEPT_BODY",BODY,{"disambiguationData":[OSD([sQuery(id+"F3.wireOp",EDGE,"E38"),sQuery(id+"F3.wireOp",EDGE,"E39"),sQuery(id+"F3.wireOp",EDGE,"E40"),sQuery(id+"F3.wireOp",EDGE,"E41")])]}),"instanceName":"1"}),"instanceName":"1"});
            transform(context, id + "F19", {"entities" : qUnion([Q0]), "transformType" : TransformType.TRANSLATION_3D, "dx" : 0 * mm, "dy" : 0 * mm, "dz" : 0 * mm, "makeCopy" : true});
        }
        {
            var Q0;
            Q0=makeQuery(id+"F12.opPattern","COPY",BODY,{"derivedFrom":makeQuery(id+"F11.opExtrude","SWEPT_BODY",BODY,{"disambiguationData":[OSD([sQuery(id+"F3.wireOp",EDGE,"E3"),sQuery(id+"F3.wireOp",EDGE,"E11"),sQuery(id+"F3.wireOp",EDGE,"E12"),sQuery(id+"F3.wireOp",EDGE,"E13"),sQuery(id+"F3.wireOp",EDGE,"E14"),sQuery(id+"F3.wireOp",EDGE,"E15"),sQuery(id+"F3.wireOp",EDGE,"E16"),sQuery(id+"F3.wireOp",EDGE,"E17"),sQuery(id+"F3.wireOp",EDGE,"E21"),sQuery(id+"F3.wireOp",EDGE,"E23"),sQuery(id+"F3.wireOp",EDGE,"E26"),sQuery(id+"F3.wireOp",EDGE,"E27"),sQuery(id+"F3.wireOp",EDGE,"E30"),sQuery(id+"F3.wireOp",EDGE,"E31"),sQuery(id+"F3.wireOp",EDGE,"E34"),sQuery(id+"F3.wireOp",EDGE,"E36"),sQuery(id+"F3.wireOp",EDGE,"E37")])]}),"instanceName":"1"});
            var Q1;
            Q1=makeQuery(id+"F17.opPattern","COPY",BODY,{"derivedFrom":makeQuery(id+"F9.opExtrude","SWEPT_BODY",BODY,{"disambiguationData":[OSD([sQuery(id+"F3.wireOp",EDGE,"E38"),sQuery(id+"F3.wireOp",EDGE,"E39"),sQuery(id+"F3.wireOp",EDGE,"E40"),sQuery(id+"F3.wireOp",EDGE,"E41")])]}),"instanceName":"1"});
            booleanBodies(context, id + "F20", {"operationType" : BooleanOperationType.SUBTRACTION, "tools" : qUnion([Q0]), "targets" : qUnion([Q1])});
        }
        {
            var Q0;
            Q0=makeQuery(id+"F14.opPattern","COPY",BODY,{"derivedFrom":makeQuery(id+"F12.opPattern","COPY",BODY,{"derivedFrom":makeQuery(id+"F11.opExtrude","SWEPT_BODY",BODY,{"disambiguationData":[OSD([sQuery(id+"F3.wireOp",EDGE,"E3"),sQuery(id+"F3.wireOp",EDGE,"E11"),sQuery(id+"F3.wireOp",EDGE,"E12"),sQuery(id+"F3.wireOp",EDGE,"E13"),sQuery(id+"F3.wireOp",EDGE,"E14"),sQuery(id+"F3.wireOp",EDGE,"E15"),sQuery(id+"F3.wireOp",EDGE,"E16"),sQuery(id+"F3.wireOp",EDGE,"E17"),sQuery(id+"F3.wireOp",EDGE,"E21"),sQuery(id+"F3.wireOp",EDGE,"E23"),sQuery(id+"F3.wireOp",EDGE,"E26"),sQuery(id+"F3.wireOp",EDGE,"E27"),sQuery(id+"F3.wireOp",EDGE,"E30"),sQuery(id+"F3.wireOp",EDGE,"E31"),sQuery(id+"F3.wireOp",EDGE,"E34"),sQuery(id+"F3.wireOp",EDGE,"E36"),sQuery(id+"F3.wireOp",EDGE,"E37")])]}),"instanceName":"1"}),"instanceName":"1"});
            var Q1;
            Q1=makeQuery(id+"F18.opPattern","COPY",BODY,{"derivedFrom":makeQuery(id+"F17.opPattern","COPY",BODY,{"derivedFrom":makeQuery(id+"F9.opExtrude","SWEPT_BODY",BODY,{"disambiguationData":[OSD([sQuery(id+"F3.wireOp",EDGE,"E38"),sQuery(id+"F3.wireOp",EDGE,"E39"),sQuery(id+"F3.wireOp",EDGE,"E40"),sQuery(id+"F3.wireOp",EDGE,"E41")])]}),"instanceName":"1"}),"instanceName":"1"});
            booleanBodies(context, id + "F21", {"operationType" : BooleanOperationType.SUBTRACTION, "tools" : qUnion([Q0]), "targets" : qUnion([Q1])});
        }
        {
            var Q0;
            Q0=makeQuery(id+"F19.opPattern","COPY",BODY,{"derivedFrom":makeQuery(id+"F18.opPattern","COPY",BODY,{"derivedFrom":makeQuery(id+"F17.opPattern","COPY",BODY,{"derivedFrom":makeQuery(id+"F9.opExtrude","SWEPT_BODY",BODY,{"disambiguationData":[OSD([sQuery(id+"F3.wireOp",EDGE,"E38"),sQuery(id+"F3.wireOp",EDGE,"E39"),sQuery(id+"F3.wireOp",EDGE,"E40"),sQuery(id+"F3.wireOp",EDGE,"E41")])]}),"instanceName":"1"}),"instanceName":"1"}),"instanceName":"1"});
            transform(context, id + "F22", {"entities" : qUnion([Q0]), "transformType" : TransformType.TRANSLATION_3D, "dx" : 0 * mm, "dy" : 0 * mm, "dz" : 0 * mm, "makeCopy" : true});
        }
        {
            var Q0;
            Q0=makeQuery(id+"F15.opPattern","COPY",BODY,{"derivedFrom":makeQuery(id+"F12.opPattern","COPY",BODY,{"derivedFrom":makeQuery(id+"F11.opExtrude","SWEPT_BODY",BODY,{"disambiguationData":[OSD([sQuery(id+"F3.wireOp",EDGE,"E3"),sQuery(id+"F3.wireOp",EDGE,"E11"),sQuery(id+"F3.wireOp",EDGE,"E12"),sQuery(id+"F3.wireOp",EDGE,"E13"),sQuery(id+"F3.wireOp",EDGE,"E14"),sQuery(id+"F3.wireOp",EDGE,"E15"),sQuery(id+"F3.wireOp",EDGE,"E16"),sQuery(id+"F3.wireOp",EDGE,"E17"),sQuery(id+"F3.wireOp",EDGE,"E21"),sQuery(id+"F3.wireOp",EDGE,"E23"),sQuery(id+"F3.wireOp",EDGE,"E26"),sQuery(id+"F3.wireOp",EDGE,"E27"),sQuery(id+"F3.wireOp",EDGE,"E30"),sQuery(id+"F3.wireOp",EDGE,"E31"),sQuery(id+"F3.wireOp",EDGE,"E34"),sQuery(id+"F3.wireOp",EDGE,"E36"),sQuery(id+"F3.wireOp",EDGE,"E37")])]}),"instanceName":"1"}),"instanceName":"1"});
            var Q1;
            Q1=makeQuery(id+"F22.opPattern","COPY",BODY,{"derivedFrom":makeQuery(id+"F19.opPattern","COPY",BODY,{"derivedFrom":makeQuery(id+"F18.opPattern","COPY",BODY,{"derivedFrom":makeQuery(id+"F17.opPattern","COPY",BODY,{"derivedFrom":makeQuery(id+"F9.opExtrude","SWEPT_BODY",BODY,{"disambiguationData":[OSD([sQuery(id+"F3.wireOp",EDGE,"E38"),sQuery(id+"F3.wireOp",EDGE,"E39"),sQuery(id+"F3.wireOp",EDGE,"E40"),sQuery(id+"F3.wireOp",EDGE,"E41")])]}),"instanceName":"1"}),"instanceName":"1"}),"instanceName":"1"}),"instanceName":"1"});
            booleanBodies(context, id + "F23", {"operationType" : BooleanOperationType.SUBTRACTION, "tools" : qUnion([Q0]), "targets" : qUnion([Q1])});
        }
        {
            var Q0;
            Q0=makeQuery(id+"F16.opPattern","COPY",BODY,{"derivedFrom":makeQuery(id+"F12.opPattern","COPY",BODY,{"derivedFrom":makeQuery(id+"F11.opExtrude","SWEPT_BODY",BODY,{"disambiguationData":[OSD([sQuery(id+"F3.wireOp",EDGE,"E3"),sQuery(id+"F3.wireOp",EDGE,"E11"),sQuery(id+"F3.wireOp",EDGE,"E12"),sQuery(id+"F3.wireOp",EDGE,"E13"),sQuery(id+"F3.wireOp",EDGE,"E14"),sQuery(id+"F3.wireOp",EDGE,"E15"),sQuery(id+"F3.wireOp",EDGE,"E16"),sQuery(id+"F3.wireOp",EDGE,"E17"),sQuery(id+"F3.wireOp",EDGE,"E21"),sQuery(id+"F3.wireOp",EDGE,"E23"),sQuery(id+"F3.wireOp",EDGE,"E26"),sQuery(id+"F3.wireOp",EDGE,"E27"),sQuery(id+"F3.wireOp",EDGE,"E30"),sQuery(id+"F3.wireOp",EDGE,"E31"),sQuery(id+"F3.wireOp",EDGE,"E34"),sQuery(id+"F3.wireOp",EDGE,"E36"),sQuery(id+"F3.wireOp",EDGE,"E37")])]}),"instanceName":"1"}),"instanceName":"1"});
            var Q1;
            Q1=makeQuery(id+"F19.opPattern","COPY",BODY,{"derivedFrom":makeQuery(id+"F18.opPattern","COPY",BODY,{"derivedFrom":makeQuery(id+"F17.opPattern","COPY",BODY,{"derivedFrom":makeQuery(id+"F9.opExtrude","SWEPT_BODY",BODY,{"disambiguationData":[OSD([sQuery(id+"F3.wireOp",EDGE,"E38"),sQuery(id+"F3.wireOp",EDGE,"E39"),sQuery(id+"F3.wireOp",EDGE,"E40"),sQuery(id+"F3.wireOp",EDGE,"E41")])]}),"instanceName":"1"}),"instanceName":"1"}),"instanceName":"1"});
            booleanBodies(context, id + "F24", {"operationType" : BooleanOperationType.SUBTRACTION, "tools" : qUnion([Q0]), "targets" : qUnion([Q1])});
        }
        {
            var Q0;
            Q0=makeQuery(id+"F11.opExtrude","SWEPT_BODY",BODY,{"disambiguationData":[OSD([sQuery(id+"F3.wireOp",EDGE,"E3"),sQuery(id+"F3.wireOp",EDGE,"E11"),sQuery(id+"F3.wireOp",EDGE,"E12"),sQuery(id+"F3.wireOp",EDGE,"E13"),sQuery(id+"F3.wireOp",EDGE,"E14"),sQuery(id+"F3.wireOp",EDGE,"E15"),sQuery(id+"F3.wireOp",EDGE,"E16"),sQuery(id+"F3.wireOp",EDGE,"E17"),sQuery(id+"F3.wireOp",EDGE,"E21"),sQuery(id+"F3.wireOp",EDGE,"E23"),sQuery(id+"F3.wireOp",EDGE,"E26"),sQuery(id+"F3.wireOp",EDGE,"E27"),sQuery(id+"F3.wireOp",EDGE,"E30"),sQuery(id+"F3.wireOp",EDGE,"E31"),sQuery(id+"F3.wireOp",EDGE,"E34"),sQuery(id+"F3.wireOp",EDGE,"E36"),sQuery(id+"F3.wireOp",EDGE,"E37")])]});
            var Q1;
            Q1=sQuery(id+"F3.wireOp",VERTEX,"E0.middle");
            transform(context, id + "F25", {"entities" : qUnion([Q0]), "transformType" : TransformType.SCALE_UNIFORMLY, "scale" : 3, "scalePoint" : qUnion([Q1]), "makeCopy" : true});
        }
        {
            var Q0;
            Q0=makeQuery(id+"F11.opExtrude","SWEPT_BODY",BODY,{"disambiguationData":[OSD([sQuery(id+"F3.wireOp",EDGE,"E3"),sQuery(id+"F3.wireOp",EDGE,"E11"),sQuery(id+"F3.wireOp",EDGE,"E12"),sQuery(id+"F3.wireOp",EDGE,"E13"),sQuery(id+"F3.wireOp",EDGE,"E14"),sQuery(id+"F3.wireOp",EDGE,"E15"),sQuery(id+"F3.wireOp",EDGE,"E16"),sQuery(id+"F3.wireOp",EDGE,"E17"),sQuery(id+"F3.wireOp",EDGE,"E21"),sQuery(id+"F3.wireOp",EDGE,"E23"),sQuery(id+"F3.wireOp",EDGE,"E26"),sQuery(id+"F3.wireOp",EDGE,"E27"),sQuery(id+"F3.wireOp",EDGE,"E30"),sQuery(id+"F3.wireOp",EDGE,"E31"),sQuery(id+"F3.wireOp",EDGE,"E34"),sQuery(id+"F3.wireOp",EDGE,"E36"),sQuery(id+"F3.wireOp",EDGE,"E37")])]});
            var Q1;
            Q1=sQuery(id+"F3.wireOp",VERTEX,"E0.middle");
            transform(context, id + "F26", {"entities" : qUnion([Q0]), "transformType" : TransformType.SCALE_UNIFORMLY, "scale" : 3.08, "scalePoint" : qUnion([Q1]), "makeCopy" : true});
        }
        {
            var Q0;
            Q0=makeQuery(id+"F17.opPattern","COPY",BODY,{"derivedFrom":makeQuery(id+"F9.opExtrude","SWEPT_BODY",BODY,{"disambiguationData":[OSD([sQuery(id+"F3.wireOp",EDGE,"E38"),sQuery(id+"F3.wireOp",EDGE,"E39"),sQuery(id+"F3.wireOp",EDGE,"E40"),sQuery(id+"F3.wireOp",EDGE,"E41")])]}),"instanceName":"1"});
            var Q1;
            Q1=qCreatedBy(makeId("Origin.pointOp"),VERTEX);
            transform(context, id + "F27", {"entities" : qUnion([Q0]), "transformType" : TransformType.SCALE_UNIFORMLY, "scale" : 3, "scalePoint" : qUnion([Q1]), "makeCopy" : true});
        }
        {
            var Q0;
            Q0=makeQuery(id+"F17.opPattern","COPY",BODY,{"derivedFrom":makeQuery(id+"F9.opExtrude","SWEPT_BODY",BODY,{"disambiguationData":[OSD([sQuery(id+"F3.wireOp",EDGE,"E38"),sQuery(id+"F3.wireOp",EDGE,"E39"),sQuery(id+"F3.wireOp",EDGE,"E40"),sQuery(id+"F3.wireOp",EDGE,"E41")])]}),"instanceName":"1"});
            var Q1;
            Q1=qCreatedBy(makeId("Origin.pointOp"),VERTEX);
            transform(context, id + "F28", {"entities" : qUnion([Q0]), "transformType" : TransformType.SCALE_UNIFORMLY, "scale" : 3.08, "scalePoint" : qUnion([Q1]), "makeCopy" : true});
        }
        {
            var Q0;
            Q0=makeQuery(id+"F17.opPattern","COPY",BODY,{"derivedFrom":makeQuery(id+"F9.opExtrude","SWEPT_BODY",BODY,{"disambiguationData":[OSD([sQuery(id+"F3.wireOp",EDGE,"E38"),sQuery(id+"F3.wireOp",EDGE,"E39"),sQuery(id+"F3.wireOp",EDGE,"E40"),sQuery(id+"F3.wireOp",EDGE,"E41")])]}),"instanceName":"1"});
            var Q1;
            Q1=qCreatedBy(makeId("Origin.pointOp"),VERTEX);
            transform(context, id + "F29", {"entities" : qUnion([Q0]), "transformType" : TransformType.SCALE_UNIFORMLY, "scale" : 3.1, "scalePoint" : qUnion([Q1]), "makeCopy" : true});
        }
        {
            var Q0;
            Q0=makeQuery(id+"F17.opPattern","COPY",BODY,{"derivedFrom":makeQuery(id+"F9.opExtrude","SWEPT_BODY",BODY,{"disambiguationData":[OSD([sQuery(id+"F3.wireOp",EDGE,"E38"),sQuery(id+"F3.wireOp",EDGE,"E39"),sQuery(id+"F3.wireOp",EDGE,"E40"),sQuery(id+"F3.wireOp",EDGE,"E41")])]}),"instanceName":"1"});
            var Q1;
            Q1=qCreatedBy(makeId("Origin.pointOp"),VERTEX);
            transform(context, id + "F30", {"entities" : qUnion([Q0]), "transformType" : TransformType.SCALE_UNIFORMLY, "scale" : 3.12, "scalePoint" : qUnion([Q1]), "makeCopy" : true});
        }
        {
            var Q0;
            Q0=makeQuery(id+"F17.opPattern","COPY",BODY,{"derivedFrom":makeQuery(id+"F9.opExtrude","SWEPT_BODY",BODY,{"disambiguationData":[OSD([sQuery(id+"F3.wireOp",EDGE,"E38"),sQuery(id+"F3.wireOp",EDGE,"E39"),sQuery(id+"F3.wireOp",EDGE,"E40"),sQuery(id+"F3.wireOp",EDGE,"E41")])]}),"instanceName":"1"});
            var Q1;
            Q1=qCreatedBy(makeId("Origin.pointOp"),VERTEX);
            transform(context, id + "F31", {"entities" : qUnion([Q0]), "transformType" : TransformType.SCALE_UNIFORMLY, "scale" : 3.15, "scalePoint" : qUnion([Q1]), "makeCopy" : true});
        }
        {
            var Q0;
            Q0=makeQuery(id+"F27.opPattern","COPY",BODY,{"derivedFrom":makeQuery(id+"F17.opPattern","COPY",BODY,{"derivedFrom":makeQuery(id+"F9.opExtrude","SWEPT_BODY",BODY,{"disambiguationData":[OSD([sQuery(id+"F3.wireOp",EDGE,"E38"),sQuery(id+"F3.wireOp",EDGE,"E39"),sQuery(id+"F3.wireOp",EDGE,"E40"),sQuery(id+"F3.wireOp",EDGE,"E41")])]}),"instanceName":"1"}),"instanceName":"1"});
            deleteBodies(context, id + "F32", {"entities" : qUnion([Q0])});
        }
        {
            var Q0;
            Q0=makeQuery(id+"F17.opPattern","COPY",BODY,{"derivedFrom":makeQuery(id+"F9.opExtrude","SWEPT_BODY",BODY,{"disambiguationData":[OSD([sQuery(id+"F3.wireOp",EDGE,"E38"),sQuery(id+"F3.wireOp",EDGE,"E39"),sQuery(id+"F3.wireOp",EDGE,"E40"),sQuery(id+"F3.wireOp",EDGE,"E41")])]}),"instanceName":"1"});
            var Q1;
            Q1=qCreatedBy(makeId("Origin.pointOp"),VERTEX);
            transform(context, id + "F33", {"entities" : qUnion([Q0]), "transformType" : TransformType.SCALE_UNIFORMLY, "scale" : 3.2, "scalePoint" : qUnion([Q1]), "makeCopy" : true});
        }
        {
            var Q0;
            Q0=makeQuery(id+"F17.opPattern","COPY",BODY,{"derivedFrom":makeQuery(id+"F9.opExtrude","SWEPT_BODY",BODY,{"disambiguationData":[OSD([sQuery(id+"F3.wireOp",EDGE,"E38"),sQuery(id+"F3.wireOp",EDGE,"E39"),sQuery(id+"F3.wireOp",EDGE,"E40"),sQuery(id+"F3.wireOp",EDGE,"E41")])]}),"instanceName":"1"});
            var Q1;
            Q1=qCreatedBy(makeId("Origin.pointOp"),VERTEX);
            transform(context, id + "F34", {"entities" : qUnion([Q0]), "transformType" : TransformType.SCALE_UNIFORMLY, "scale" : 3.3, "scalePoint" : qUnion([Q1]), "makeCopy" : true});
        }
        {
            var Q0;
            Q0=makeQuery(id+"F29.opPattern","COPY",FACE,{"derivedFrom":makeQuery(id+"F17.opPattern","COPY",FACE,{"derivedFrom":makeQuery(id+"F9.opExtrude","CAP_FACE",FACE,{"disambiguationData":[OSD([sQuery(id+"F3.wireOp",EDGE,"E38"),sQuery(id+"F3.wireOp",EDGE,"E39"),sQuery(id+"F3.wireOp",EDGE,"E40"),sQuery(id+"F3.wireOp",EDGE,"E41")])],"isStart":false}),"instanceName":"1"}),"instanceName":"1"});
            extrude(context, id + "F35", {"entities" : qUnion([Q0]), "operationType" : NewBodyOperationType.REMOVE, "oppositeDirection" : true, "depth" : 25 * mm, "offsetDistance" : 25 * mm});
        }
        {
            var Q0;
            Q0=makeQuery(id+"F30.opPattern","COPY",FACE,{"derivedFrom":makeQuery(id+"F17.opPattern","COPY",FACE,{"derivedFrom":makeQuery(id+"F9.opExtrude","CAP_FACE",FACE,{"disambiguationData":[OSD([sQuery(id+"F3.wireOp",EDGE,"E38"),sQuery(id+"F3.wireOp",EDGE,"E39"),sQuery(id+"F3.wireOp",EDGE,"E40"),sQuery(id+"F3.wireOp",EDGE,"E41")])],"isStart":false}),"instanceName":"1"}),"instanceName":"1"});
            extrude(context, id + "F36", {"entities" : qUnion([Q0]), "operationType" : NewBodyOperationType.REMOVE, "oppositeDirection" : true, "depth" : 25 * mm, "offsetDistance" : 25 * mm});
        }
        {
            var Q0;
            Q0=makeQuery(id+"F31.opPattern","COPY",FACE,{"derivedFrom":makeQuery(id+"F17.opPattern","COPY",FACE,{"derivedFrom":makeQuery(id+"F9.opExtrude","CAP_FACE",FACE,{"disambiguationData":[OSD([sQuery(id+"F3.wireOp",EDGE,"E38"),sQuery(id+"F3.wireOp",EDGE,"E39"),sQuery(id+"F3.wireOp",EDGE,"E40"),sQuery(id+"F3.wireOp",EDGE,"E41")])],"isStart":false}),"instanceName":"1"}),"instanceName":"1"});
            extrude(context, id + "F37", {"entities" : qUnion([Q0]), "operationType" : NewBodyOperationType.REMOVE, "oppositeDirection" : true, "depth" : 25 * mm, "offsetDistance" : 25 * mm});
        }
        {
            var Q0;
            Q0=makeQuery(id+"F33.opPattern","COPY",FACE,{"derivedFrom":makeQuery(id+"F17.opPattern","COPY",FACE,{"derivedFrom":makeQuery(id+"F9.opExtrude","CAP_FACE",FACE,{"disambiguationData":[OSD([sQuery(id+"F3.wireOp",EDGE,"E38"),sQuery(id+"F3.wireOp",EDGE,"E39"),sQuery(id+"F3.wireOp",EDGE,"E40"),sQuery(id+"F3.wireOp",EDGE,"E41")])],"isStart":false}),"instanceName":"1"}),"instanceName":"1"});
            extrude(context, id + "F38", {"entities" : qUnion([Q0]), "operationType" : NewBodyOperationType.REMOVE, "oppositeDirection" : true, "depth" : 25 * mm, "offsetDistance" : 25 * mm});
        }
        {
            var Q0;
            Q0=makeQuery(id+"F34.opPattern","COPY",FACE,{"derivedFrom":makeQuery(id+"F17.opPattern","COPY",FACE,{"derivedFrom":makeQuery(id+"F9.opExtrude","CAP_FACE",FACE,{"disambiguationData":[OSD([sQuery(id+"F3.wireOp",EDGE,"E38"),sQuery(id+"F3.wireOp",EDGE,"E39"),sQuery(id+"F3.wireOp",EDGE,"E40"),sQuery(id+"F3.wireOp",EDGE,"E41")])],"isStart":false}),"instanceName":"1"}),"instanceName":"1"});
            extrude(context, id + "F39", {"entities" : qUnion([Q0]), "operationType" : NewBodyOperationType.REMOVE, "oppositeDirection" : true, "depth" : 25 * mm, "offsetDistance" : 25 * mm});
        }
        {
            var Q0;
            Q0=makeQuery(id+"F11.opExtrude","SWEPT_BODY",BODY,{"disambiguationData":[OSD([sQuery(id+"F3.wireOp",EDGE,"E3"),sQuery(id+"F3.wireOp",EDGE,"E11"),sQuery(id+"F3.wireOp",EDGE,"E12"),sQuery(id+"F3.wireOp",EDGE,"E13"),sQuery(id+"F3.wireOp",EDGE,"E14"),sQuery(id+"F3.wireOp",EDGE,"E15"),sQuery(id+"F3.wireOp",EDGE,"E16"),sQuery(id+"F3.wireOp",EDGE,"E17"),sQuery(id+"F3.wireOp",EDGE,"E21"),sQuery(id+"F3.wireOp",EDGE,"E23"),sQuery(id+"F3.wireOp",EDGE,"E26"),sQuery(id+"F3.wireOp",EDGE,"E27"),sQuery(id+"F3.wireOp",EDGE,"E30"),sQuery(id+"F3.wireOp",EDGE,"E31"),sQuery(id+"F3.wireOp",EDGE,"E34"),sQuery(id+"F3.wireOp",EDGE,"E36"),sQuery(id+"F3.wireOp",EDGE,"E37")])]});
            var Q1;
            Q1=qCreatedBy(makeId("Origin.pointOp"),VERTEX);
            transform(context, id + "F40", {"entities" : qUnion([Q0]), "transformType" : TransformType.SCALE_UNIFORMLY, "scale" : 3.1, "scalePoint" : qUnion([Q1]), "makeCopy" : true});
        }
    });
